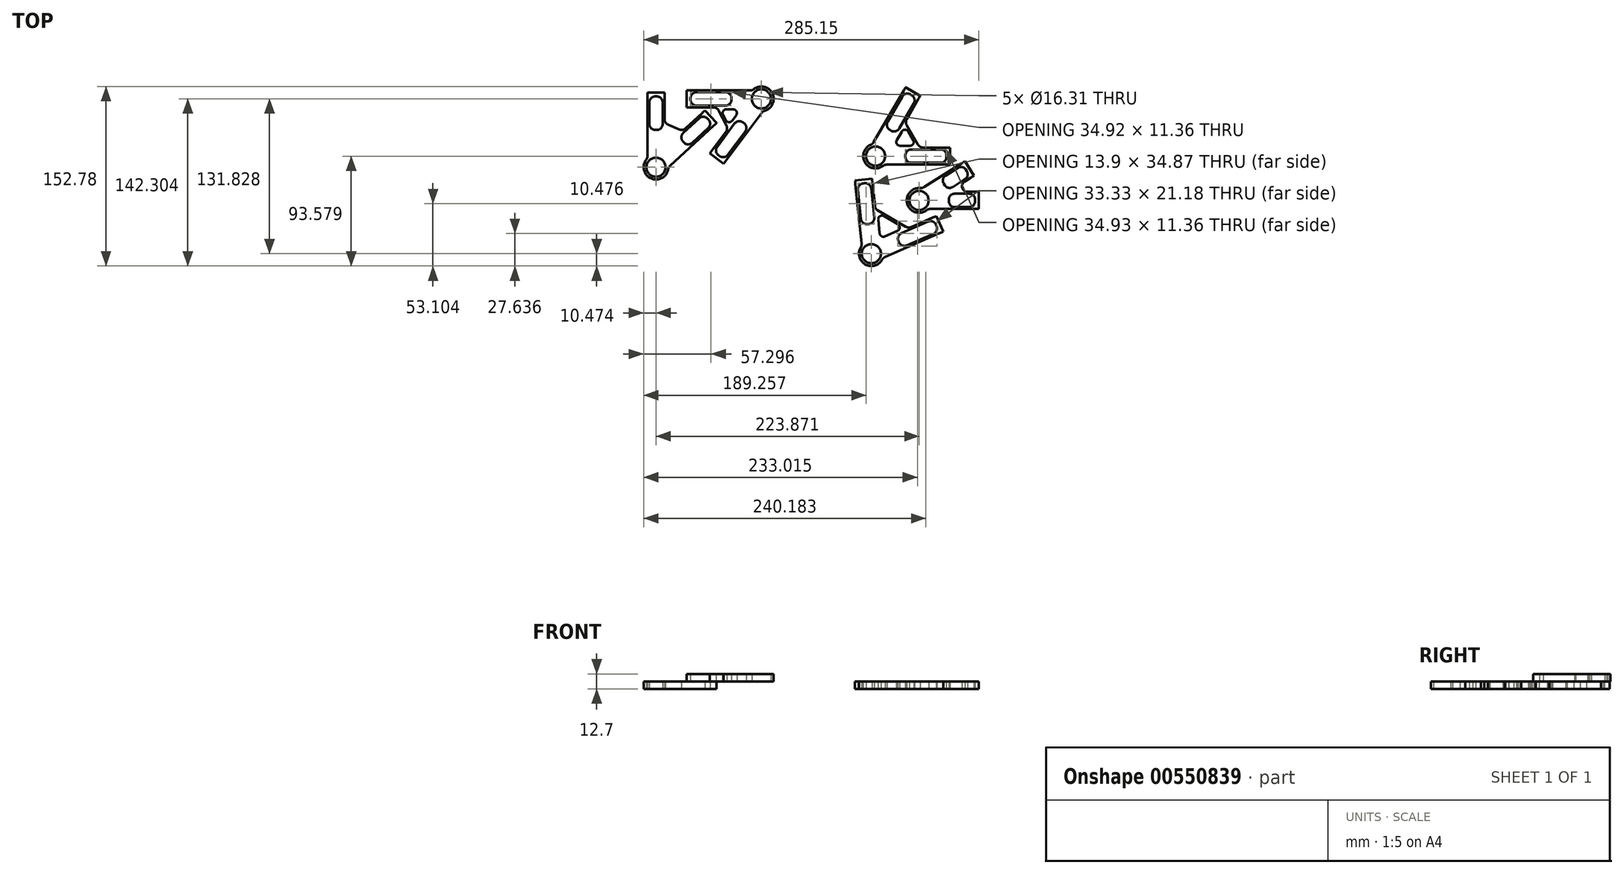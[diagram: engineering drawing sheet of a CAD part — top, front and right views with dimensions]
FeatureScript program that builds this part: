
annotation { "Feature Type Name" : "Feature", "Feature Type Description" : "" }
export const myFeature = defineFeature(function(context is Context, id is Id, definition is map)
    precondition{}
    {
        {
            var Q0;
            Q0=qCreatedBy(makeId("Top.planeOp"),FACE);
            var sketch = newSketch(context, id + "F0", { "sketchPlane" : qUnion([Q0])});
            skLineSegment(sketch, "E0", {"start": v(266.5, 117.67) * mm, "end": v(266.5, 132.21) * mm});
            skLineSegment(sketch, "E1", {"start": v(262.48, 146.06) * mm, "end": v(254.68, 158.33) * mm});
            skLineSegment(sketch, "E2", {"start": v(236.2, 98.34) * mm, "end": v(230.38, 111.66) * mm});
            skLineSegment(sketch, "E3", {"start": v(175.69, 143.49) * mm, "end": v(161.23, 141.97) * mm});
            skLineSegment(sketch, "E4", {"start": v(242.18, 155.4) * mm, "end": v(242.18, 169.95) * mm});
            skLineSegment(sketch, "E5", {"start": v(216.73, 214.04) * mm, "end": v(204.14, 221.3) * mm});
            skLineSegment(sketch, "E6", {"start": v(-0.9, 216.73) * mm, "end": v(-15.44, 216.73) * mm});
            skLineSegment(sketch, "E7", {"start": v(43.43, 190.95) * mm, "end": v(33.57, 201.64) * mm});
            skLineSegment(sketch, "E8", {"start": v(185.25, 66.4) * mm, "end": v(185.8, 67.33) * mm});
            skLineSegment(sketch, "E9", {"start": v(185.8, 67.33) * mm, "end": v(186.27, 68.16) * mm});
            skLineSegment(sketch, "E10", {"start": v(186.27, 68.16) * mm, "end": v(186.62, 68.77) * mm});
            skLineSegment(sketch, "E11", {"start": v(186.62, 68.77) * mm, "end": v(186.81, 69.1) * mm});
            skLineSegment(sketch, "E12", {"start": v(186.81, 69.1) * mm, "end": v(186.84, 69.14) * mm});
            skLineSegment(sketch, "E13", {"start": v(254.51, 141) * mm, "end": v(259.8, 144.36) * mm});
            skLineSegment(sketch, "E14", {"start": v(263.33, 132.21) * mm, "end": v(257.07, 132.21) * mm});
            skLineSegment(sketch, "E15", {"start": v(245.87, 130.63) * mm, "end": v(258.57, 130.63) * mm});
            skLineSegment(sketch, "E16", {"start": v(241.1, 124.02) * mm, "end": v(241.1, 125.86) * mm});
            skLineSegment(sketch, "E17", {"start": v(258.57, 119.26) * mm, "end": v(245.87, 119.26) * mm});
            skLineSegment(sketch, "E18", {"start": v(225.59, 117.67) * mm, "end": v(263.33, 117.67) * mm});
            skLineSegment(sketch, "E19", {"start": v(252, 156.63) * mm, "end": v(220.15, 136.38) * mm});
            skLineSegment(sketch, "E20", {"start": v(238.11, 145.92) * mm, "end": v(248.83, 152.73) * mm});
            skLineSegment(sketch, "E21", {"start": v(237.63, 137.8) * mm, "end": v(236.65, 139.34) * mm});
            skLineSegment(sketch, "E22", {"start": v(254.93, 143.14) * mm, "end": v(244.2, 136.33) * mm});
            skLineSegment(sketch, "E23", {"start": v(263.33, 124.02) * mm, "end": v(263.33, 125.86) * mm});
            skLineSegment(sketch, "E24", {"start": v(266.5, 132.21) * mm, "end": v(263.33, 132.21) * mm});
            skLineSegment(sketch, "E25", {"start": v(266.5, 117.67) * mm, "end": v(263.33, 117.67) * mm});
            skLineSegment(sketch, "E26", {"start": v(256.4, 149.71) * mm, "end": v(255.4, 151.27) * mm});
            skLineSegment(sketch, "E27", {"start": v(262.48, 146.06) * mm, "end": v(262.44, 146.03) * mm});
            skLineSegment(sketch, "E28", {"start": v(262.44, 146.03) * mm, "end": v(262.12, 145.83) * mm});
            skLineSegment(sketch, "E29", {"start": v(262.12, 145.83) * mm, "end": v(261.52, 145.45) * mm});
            skLineSegment(sketch, "E30", {"start": v(261.52, 145.45) * mm, "end": v(260.71, 144.94) * mm});
            skLineSegment(sketch, "E31", {"start": v(260.71, 144.94) * mm, "end": v(259.8, 144.36) * mm});
            skLineSegment(sketch, "E32", {"start": v(252, 156.63) * mm, "end": v(252.92, 157.2) * mm});
            skLineSegment(sketch, "E33", {"start": v(252.92, 157.2) * mm, "end": v(253.72, 157.72) * mm});
            skLineSegment(sketch, "E34", {"start": v(253.72, 157.72) * mm, "end": v(254.32, 158.1) * mm});
            skLineSegment(sketch, "E35", {"start": v(254.32, 158.1) * mm, "end": v(254.64, 158.3) * mm});
            skLineSegment(sketch, "E36", {"start": v(254.64, 158.3) * mm, "end": v(254.68, 158.33) * mm});
            skLineSegment(sketch, "E37", {"start": v(236.2, 98.34) * mm, "end": v(236.15, 98.32) * mm});
            skLineSegment(sketch, "E38", {"start": v(236.15, 98.32) * mm, "end": v(235.8, 98.17) * mm});
            skLineSegment(sketch, "E39", {"start": v(235.8, 98.17) * mm, "end": v(235.16, 97.88) * mm});
            skLineSegment(sketch, "E40", {"start": v(235.16, 97.88) * mm, "end": v(234.28, 97.5) * mm});
            skLineSegment(sketch, "E41", {"start": v(234.28, 97.5) * mm, "end": v(233.29, 97.07) * mm});
            skLineSegment(sketch, "E42", {"start": v(230.62, 103.18) * mm, "end": v(230.14, 104.28) * mm});
            skLineSegment(sketch, "E43", {"start": v(227.47, 110.39) * mm, "end": v(228.46, 110.82) * mm});
            skLineSegment(sketch, "E44", {"start": v(228.46, 110.82) * mm, "end": v(229.34, 111.2) * mm});
            skLineSegment(sketch, "E45", {"start": v(229.34, 111.2) * mm, "end": v(229.99, 111.49) * mm});
            skLineSegment(sketch, "E46", {"start": v(229.99, 111.49) * mm, "end": v(230.33, 111.64) * mm});
            skLineSegment(sketch, "E47", {"start": v(230.33, 111.64) * mm, "end": v(230.38, 111.66) * mm});
            skLineSegment(sketch, "E48", {"start": v(161.56, 138.81) * mm, "end": v(166.88, 88.23) * mm});
            skLineSegment(sketch, "E49", {"start": v(166.26, 109.3) * mm, "end": v(163.67, 133.92) * mm});
            skLineSegment(sketch, "E50", {"start": v(171.84, 104.77) * mm, "end": v(173.04, 104.9) * mm});
            skLineSegment(sketch, "E51", {"start": v(174.97, 135.11) * mm, "end": v(177.56, 110.48) * mm});
            skLineSegment(sketch, "E52", {"start": v(178.13, 120.24) * mm, "end": v(176.02, 140.33) * mm});
            skLineSegment(sketch, "E53", {"start": v(204.37, 102.57) * mm, "end": v(180.63, 116.38) * mm});
            skLineSegment(sketch, "E54", {"start": v(200.75, 96.99) * mm, "end": v(223.45, 106.9) * mm});
            skLineSegment(sketch, "E55", {"start": v(198.13, 90.3) * mm, "end": v(198.61, 89.2) * mm});
            skLineSegment(sketch, "E56", {"start": v(228, 96.49) * mm, "end": v(205.3, 86.57) * mm});
            skLineSegment(sketch, "E57", {"start": v(185.72, 111.58) * mm, "end": v(197.68, 104.62) * mm});
            skLineSegment(sketch, "E58", {"start": v(182.19, 96.85) * mm, "end": v(180.96, 108.5) * mm});
            skLineSegment(sketch, "E59", {"start": v(197.35, 98.97) * mm, "end": v(186.62, 94.28) * mm});
            skLineSegment(sketch, "E60", {"start": v(227.47, 110.39) * mm, "end": v(208.95, 102.3) * mm});
            skLineSegment(sketch, "E61", {"start": v(186.68, 76.7) * mm, "end": v(233.29, 97.07) * mm});
            skLineSegment(sketch, "E62", {"start": v(175.69, 143.49) * mm, "end": v(175.7, 143.44) * mm});
            skLineSegment(sketch, "E63", {"start": v(175.7, 143.44) * mm, "end": v(175.73, 143.07) * mm});
            skLineSegment(sketch, "E64", {"start": v(175.73, 143.07) * mm, "end": v(175.8, 142.36) * mm});
            skLineSegment(sketch, "E65", {"start": v(175.8, 142.36) * mm, "end": v(175.9, 141.41) * mm});
            skLineSegment(sketch, "E66", {"start": v(175.9, 141.41) * mm, "end": v(176.02, 140.33) * mm});
            skLineSegment(sketch, "E67", {"start": v(169.4, 139.63) * mm, "end": v(168.2, 139.5) * mm});
            skLineSegment(sketch, "E68", {"start": v(161.56, 138.81) * mm, "end": v(161.45, 139.9) * mm});
            skLineSegment(sketch, "E69", {"start": v(161.45, 139.9) * mm, "end": v(161.35, 140.84) * mm});
            skLineSegment(sketch, "E70", {"start": v(161.35, 140.84) * mm, "end": v(161.28, 141.55) * mm});
            skLineSegment(sketch, "E71", {"start": v(161.28, 141.55) * mm, "end": v(161.24, 141.92) * mm});
            skLineSegment(sketch, "E72", {"start": v(161.24, 141.92) * mm, "end": v(161.23, 141.97) * mm});
            skLineSegment(sketch, "E73", {"start": v(242.18, 155.4) * mm, "end": v(239, 155.4) * mm});
            skLineSegment(sketch, "E74", {"start": v(239, 162.08) * mm, "end": v(239, 163.28) * mm});
            skLineSegment(sketch, "E75", {"start": v(239, 169.95) * mm, "end": v(242.18, 169.95) * mm});
            skLineSegment(sketch, "E76", {"start": v(202.55, 218.56) * mm, "end": v(177.12, 174.5) * mm});
            skLineSegment(sketch, "E77", {"start": v(189, 191.92) * mm, "end": v(201.38, 213.36) * mm});
            skLineSegment(sketch, "E78", {"start": v(190.86, 184.98) * mm, "end": v(191.9, 184.38) * mm});
            skLineSegment(sketch, "E79", {"start": v(211.22, 207.68) * mm, "end": v(198.84, 186.23) * mm});
            skLineSegment(sketch, "E80", {"start": v(205.22, 194.1) * mm, "end": v(215.14, 211.29) * mm});
            skLineSegment(sketch, "E81", {"start": v(214.76, 172.49) * mm, "end": v(205.22, 189.02) * mm});
            skLineSegment(sketch, "E82", {"start": v(209.16, 168.36) * mm, "end": v(233.93, 168.36) * mm});
            skLineSegment(sketch, "E83", {"start": v(204.08, 163.28) * mm, "end": v(204.08, 162.08) * mm});
            skLineSegment(sketch, "E84", {"start": v(233.93, 157) * mm, "end": v(209.16, 157) * mm});
            skLineSegment(sketch, "E85", {"start": v(206.5, 183.62) * mm, "end": v(210.73, 176.3) * mm});
            skLineSegment(sketch, "E86", {"start": v(196.77, 176.3) * mm, "end": v(201, 183.62) * mm});
            skLineSegment(sketch, "E87", {"start": v(207.98, 171.54) * mm, "end": v(199.52, 171.54) * mm});
            skLineSegment(sketch, "E88", {"start": v(239, 169.95) * mm, "end": v(219.16, 169.95) * mm});
            skLineSegment(sketch, "E89", {"start": v(188.14, 155.4) * mm, "end": v(239, 155.4) * mm});
            skLineSegment(sketch, "E90", {"start": v(216.73, 214.04) * mm, "end": v(216.7, 214) * mm});
            skLineSegment(sketch, "E91", {"start": v(216.7, 214) * mm, "end": v(216.51, 213.67) * mm});
            skLineSegment(sketch, "E92", {"start": v(216.51, 213.67) * mm, "end": v(216.16, 213.05) * mm});
            skLineSegment(sketch, "E93", {"start": v(216.16, 213.05) * mm, "end": v(215.68, 212.23) * mm});
            skLineSegment(sketch, "E94", {"start": v(215.68, 212.23) * mm, "end": v(215.14, 211.29) * mm});
            skLineSegment(sketch, "E95", {"start": v(209.36, 214.62) * mm, "end": v(208.32, 215.22) * mm});
            skLineSegment(sketch, "E96", {"start": v(202.55, 218.56) * mm, "end": v(203.1, 219.5) * mm});
            skLineSegment(sketch, "E97", {"start": v(203.1, 219.5) * mm, "end": v(203.57, 220.32) * mm});
            skLineSegment(sketch, "E98", {"start": v(203.57, 220.32) * mm, "end": v(203.92, 220.94) * mm});
            skLineSegment(sketch, "E99", {"start": v(203.92, 220.94) * mm, "end": v(204.11, 221.26) * mm});
            skLineSegment(sketch, "E100", {"start": v(204.11, 221.26) * mm, "end": v(204.14, 221.3) * mm});
            skLineSegment(sketch, "E101", {"start": v(-15.44, 213.56) * mm, "end": v(-15.44, 162.7) * mm});
            skLineSegment(sketch, "E102", {"start": v(-13.85, 190.06) * mm, "end": v(-13.85, 208.48) * mm});
            skLineSegment(sketch, "E103", {"start": v(-8.77, 184.98) * mm, "end": v(-7.56, 184.98) * mm});
            skLineSegment(sketch, "E104", {"start": v(-2.48, 208.48) * mm, "end": v(-2.48, 190.06) * mm});
            skLineSegment(sketch, "E105", {"start": v(-0.9, 194.1) * mm, "end": v(-0.9, 213.56) * mm});
            skLineSegment(sketch, "E106", {"start": v(11.45, 185.37) * mm, "end": v(2.15, 189.44) * mm});
            skLineSegment(sketch, "E107", {"start": v(31.24, 199.48) * mm, "end": v(16.94, 186.29) * mm});
            skLineSegment(sketch, "E108", {"start": v(15.05, 182.38) * mm, "end": v(28.58, 194.87) * mm});
            skLineSegment(sketch, "E109", {"start": v(14.76, 175.2) * mm, "end": v(15.58, 174.32) * mm});
            skLineSegment(sketch, "E110", {"start": v(36.29, 186.52) * mm, "end": v(22.75, 174.03) * mm});
            skLineSegment(sketch, "E111", {"start": v(3.72, 154.3) * mm, "end": v(41.1, 188.8) * mm});
            skLineSegment(sketch, "E112", {"start": v(-15.44, 213.56) * mm, "end": v(-15.44, 216.73) * mm});
            skLineSegment(sketch, "E113", {"start": v(-0.9, 216.73) * mm, "end": v(-0.9, 213.56) * mm});
            skLineSegment(sketch, "E114", {"start": v(-7.56, 213.56) * mm, "end": v(-8.77, 213.56) * mm});
            skLineSegment(sketch, "E115", {"start": v(36.58, 193.7) * mm, "end": v(35.76, 194.58) * mm});
            skLineSegment(sketch, "E116", {"start": v(31.24, 199.48) * mm, "end": v(32.04, 200.22) * mm});
            skLineSegment(sketch, "E117", {"start": v(32.04, 200.22) * mm, "end": v(32.74, 200.87) * mm});
            skLineSegment(sketch, "E118", {"start": v(32.74, 200.87) * mm, "end": v(33.26, 201.35) * mm});
            skLineSegment(sketch, "E119", {"start": v(33.26, 201.35) * mm, "end": v(33.54, 201.6) * mm});
            skLineSegment(sketch, "E120", {"start": v(33.54, 201.6) * mm, "end": v(33.57, 201.64) * mm});
            skLineSegment(sketch, "E121", {"start": v(43.43, 190.95) * mm, "end": v(43.4, 190.92) * mm});
            skLineSegment(sketch, "E122", {"start": v(43.4, 190.92) * mm, "end": v(43.12, 190.66) * mm});
            skLineSegment(sketch, "E123", {"start": v(43.12, 190.66) * mm, "end": v(42.6, 190.18) * mm});
            skLineSegment(sketch, "E124", {"start": v(42.6, 190.18) * mm, "end": v(41.9, 189.53) * mm});
            skLineSegment(sketch, "E125", {"start": v(41.9, 189.53) * mm, "end": v(41.1, 188.8) * mm});
            skCircle(sketch, "E126", {"center": v(-8.17, 153.23) * mm, "radius": 8.16 * mm});
            skArc(sketch, "E127", {"start": v(254.93, 143.14) * mm, "mid": v(257.02, 146.12) * mm, "end": v(256.4, 149.71) * mm});
            skArc(sketch, "E128", {"start": v(254.51, 141) * mm, "mid": v(252.5, 135.65) * mm, "end": v(257.07, 132.21) * mm});
            skArc(sketch, "E129", {"start": v(263.33, 125.86) * mm, "mid": v(261.94, 129.23) * mm, "end": v(258.57, 130.63) * mm});
            skArc(sketch, "E130", {"start": v(245.87, 130.63) * mm, "mid": v(242.5, 129.23) * mm, "end": v(241.1, 125.86) * mm});
            skArc(sketch, "E131", {"start": v(241.1, 124.02) * mm, "mid": v(242.5, 120.66) * mm, "end": v(245.87, 119.26) * mm});
            skArc(sketch, "E132", {"start": v(258.57, 119.26) * mm, "mid": v(261.94, 120.66) * mm, "end": v(263.33, 124.02) * mm});
            skArc(sketch, "E133", {"start": v(225.59, 117.67) * mm, "mid": v(223.63, 117.36) * mm, "end": v(221.86, 116.46) * mm});
            skArc(sketch, "E134", {"start": v(216.35, 135.4) * mm, "mid": v(205.64, 122.02) * mm, "end": v(221.86, 116.46) * mm});
            skArc(sketch, "E135", {"start": v(216.35, 135.4) * mm, "mid": v(218.33, 135.6) * mm, "end": v(220.15, 136.38) * mm});
            skArc(sketch, "E136", {"start": v(255.4, 151.27) * mm, "mid": v(252.42, 153.36) * mm, "end": v(248.83, 152.73) * mm});
            skArc(sketch, "E137", {"start": v(238.11, 145.92) * mm, "mid": v(236.02, 142.94) * mm, "end": v(236.65, 139.34) * mm});
            skArc(sketch, "E138", {"start": v(237.63, 137.8) * mm, "mid": v(240.62, 135.7) * mm, "end": v(244.2, 136.33) * mm});
            skArc(sketch, "E139", {"start": v(166.16, 85.04) * mm, "mid": v(166.78, 86.58) * mm, "end": v(166.88, 88.23) * mm});
            skArc(sketch, "E140", {"start": v(168.2, 139.5) * mm, "mid": v(164.78, 137.65) * mm, "end": v(163.67, 133.92) * mm});
            skArc(sketch, "E141", {"start": v(166.26, 109.3) * mm, "mid": v(168.12, 105.88) * mm, "end": v(171.84, 104.77) * mm});
            skArc(sketch, "E142", {"start": v(173.04, 104.9) * mm, "mid": v(176.46, 106.76) * mm, "end": v(177.56, 110.48) * mm});
            skArc(sketch, "E143", {"start": v(174.97, 135.11) * mm, "mid": v(173.12, 138.53) * mm, "end": v(169.4, 139.63) * mm});
            skArc(sketch, "E144", {"start": v(178.13, 120.24) * mm, "mid": v(178.92, 118.01) * mm, "end": v(180.63, 116.38) * mm});
            skArc(sketch, "E145", {"start": v(204.37, 102.57) * mm, "mid": v(206.63, 101.88) * mm, "end": v(208.95, 102.3) * mm});
            skArc(sketch, "E146", {"start": v(200.75, 96.99) * mm, "mid": v(198.06, 94.18) * mm, "end": v(198.13, 90.3) * mm});
            skArc(sketch, "E147", {"start": v(198.61, 89.2) * mm, "mid": v(201.42, 86.5) * mm, "end": v(205.3, 86.57) * mm});
            skArc(sketch, "E148", {"start": v(228, 96.49) * mm, "mid": v(230.7, 99.29) * mm, "end": v(230.62, 103.18) * mm});
            skArc(sketch, "E149", {"start": v(186.68, 76.7) * mm, "mid": v(185.3, 75.8) * mm, "end": v(184.27, 74.5) * mm});
            skArc(sketch, "E150", {"start": v(166.16, 85.04) * mm, "mid": v(169.83, 70.52) * mm, "end": v(184.27, 74.5) * mm});
            skArc(sketch, "E151", {"start": v(197.35, 98.97) * mm, "mid": v(199.25, 101.7) * mm, "end": v(197.68, 104.62) * mm});
            skArc(sketch, "E152", {"start": v(185.72, 111.58) * mm, "mid": v(182.4, 111.5) * mm, "end": v(180.96, 108.5) * mm});
            skArc(sketch, "E153", {"start": v(182.19, 96.85) * mm, "mid": v(183.75, 94.44) * mm, "end": v(186.62, 94.28) * mm});
            skArc(sketch, "E154", {"start": v(230.14, 104.28) * mm, "mid": v(227.33, 106.97) * mm, "end": v(223.45, 106.9) * mm});
            skCircle(sketch, "E155", {"center": v(178.68, 162.68) * mm, "radius": 8.16 * mm});
            skCircle(sketch, "E156", {"center": v(215.7, 124.94) * mm, "radius": 8.16 * mm});
            skArc(sketch, "E157", {"start": v(174.66, 172.36) * mm, "mid": v(176.07, 173.23) * mm, "end": v(177.12, 174.5) * mm});
            skArc(sketch, "E158", {"start": v(208.32, 215.22) * mm, "mid": v(204.47, 215.73) * mm, "end": v(201.38, 213.36) * mm});
            skArc(sketch, "E159", {"start": v(189, 191.92) * mm, "mid": v(188.5, 188.06) * mm, "end": v(190.86, 184.98) * mm});
            skArc(sketch, "E160", {"start": v(191.9, 184.38) * mm, "mid": v(195.76, 183.87) * mm, "end": v(198.84, 186.23) * mm});
            skArc(sketch, "E161", {"start": v(211.22, 207.68) * mm, "mid": v(211.73, 211.54) * mm, "end": v(209.36, 214.62) * mm});
            skArc(sketch, "E162", {"start": v(205.22, 194.1) * mm, "mid": v(204.54, 191.56) * mm, "end": v(205.22, 189.02) * mm});
            skArc(sketch, "E163", {"start": v(214.76, 172.49) * mm, "mid": v(216.62, 170.63) * mm, "end": v(219.16, 169.95) * mm});
            skArc(sketch, "E164", {"start": v(239, 163.28) * mm, "mid": v(237.52, 166.87) * mm, "end": v(233.93, 168.36) * mm});
            skArc(sketch, "E165", {"start": v(209.16, 168.36) * mm, "mid": v(205.57, 166.87) * mm, "end": v(204.08, 163.28) * mm});
            skArc(sketch, "E166", {"start": v(204.08, 162.08) * mm, "mid": v(205.57, 158.49) * mm, "end": v(209.16, 157) * mm});
            skArc(sketch, "E167", {"start": v(233.93, 157) * mm, "mid": v(237.52, 158.49) * mm, "end": v(239, 162.08) * mm});
            skArc(sketch, "E168", {"start": v(188.14, 155.4) * mm, "mid": v(186.51, 155.14) * mm, "end": v(185.05, 154.36) * mm});
            skArc(sketch, "E169", {"start": v(174.66, 172.36) * mm, "mid": v(169.6, 157.44) * mm, "end": v(185.05, 154.36) * mm});
            skArc(sketch, "E170", {"start": v(207.98, 171.54) * mm, "mid": v(210.73, 173.12) * mm, "end": v(210.73, 176.3) * mm});
            skArc(sketch, "E171", {"start": v(206.5, 183.62) * mm, "mid": v(203.75, 185.2) * mm, "end": v(201, 183.62) * mm});
            skArc(sketch, "E172", {"start": v(196.77, 176.3) * mm, "mid": v(196.77, 173.12) * mm, "end": v(199.52, 171.54) * mm});
            skCircle(sketch, "E173", {"center": v(175.1, 79.58) * mm, "radius": 8.16 * mm});
            skArc(sketch, "E174", {"start": v(-16.48, 159.6) * mm, "mid": v(-15.7, 161.06) * mm, "end": v(-15.44, 162.7) * mm});
            skArc(sketch, "E175", {"start": v(-8.77, 213.56) * mm, "mid": v(-12.36, 212.07) * mm, "end": v(-13.85, 208.48) * mm});
            skArc(sketch, "E176", {"start": v(-13.85, 190.06) * mm, "mid": v(-12.36, 186.47) * mm, "end": v(-8.77, 184.98) * mm});
            skArc(sketch, "E177", {"start": v(-7.56, 184.98) * mm, "mid": v(-3.97, 186.47) * mm, "end": v(-2.48, 190.06) * mm});
            skArc(sketch, "E178", {"start": v(-2.48, 208.48) * mm, "mid": v(-3.97, 212.07) * mm, "end": v(-7.56, 213.56) * mm});
            skArc(sketch, "E179", {"start": v(-0.9, 194.1) * mm, "mid": v(-0.07, 191.32) * mm, "end": v(2.15, 189.44) * mm});
            skArc(sketch, "E180", {"start": v(11.45, 185.37) * mm, "mid": v(14.33, 185.01) * mm, "end": v(16.94, 186.29) * mm});
            skArc(sketch, "E181", {"start": v(35.76, 194.58) * mm, "mid": v(32.23, 196.21) * mm, "end": v(28.58, 194.87) * mm});
            skArc(sketch, "E182", {"start": v(15.05, 182.38) * mm, "mid": v(13.42, 178.85) * mm, "end": v(14.76, 175.2) * mm});
            skArc(sketch, "E183", {"start": v(15.58, 174.32) * mm, "mid": v(19.1, 172.69) * mm, "end": v(22.75, 174.03) * mm});
            skArc(sketch, "E184", {"start": v(36.29, 186.52) * mm, "mid": v(37.92, 190.05) * mm, "end": v(36.58, 193.7) * mm});
            skArc(sketch, "E185", {"start": v(3.72, 154.3) * mm, "mid": v(2.7, 153) * mm, "end": v(2.16, 151.44) * mm});
            skArc(sketch, "E186", {"start": v(-16.48, 159.6) * mm, "mid": v(-12.37, 143.63) * mm, "end": v(2.16, 151.44) * mm});
            skSolve(sketch);
        }
        {
            var Q0;
            Q0=makeQuery(id+"F0.imprint","IMPRINT",FACE,{"disambiguationData":[TD([[makeQuery(id+"F0.imprint","IMPRINT",EDGE,{"derivedFrom":sQuery(id+"F0.wireOp",EDGE,"E6")}),1.0]])]});
            var Q1;
            Q1=makeQuery(id+"F0.imprint","IMPRINT",FACE,{"disambiguationData":[TD([[makeQuery(id+"F0.imprint","IMPRINT",EDGE,{"derivedFrom":sQuery(id+"F0.wireOp",EDGE,"E4")}),1.0]])]});
            var Q2;
            Q2=makeQuery(id+"F0.imprint","IMPRINT",FACE,{"disambiguationData":[TD([[makeQuery(id+"F0.imprint","IMPRINT",EDGE,{"derivedFrom":sQuery(id+"F0.wireOp",EDGE,"E0")}),1.0]])]});
            var Q3;
            Q3=makeQuery(id+"F0.imprint","IMPRINT",FACE,{"disambiguationData":[TD([[makeQuery(id+"F0.imprint","IMPRINT",EDGE,{"derivedFrom":sQuery(id+"F0.wireOp",EDGE,"E2")}),1.0]])]});
            extrude(context, id + "F1", {"entities" : qUnion([Q0, Q1, Q2, Q3]), "depth" : 6.35 * mm, "offsetDistance" : 25.4 * mm});
        }
        {
            var Q0;
            Q0=makeQuery(id+"F1.opExtrude","CAP_FACE",FACE,{"disambiguationData":[OSD([sQuery(id+"F0.wireOp",EDGE,"E6"),sQuery(id+"F0.wireOp",EDGE,"E7"),sQuery(id+"F0.wireOp",EDGE,"E101"),sQuery(id+"F0.wireOp",EDGE,"E102"),sQuery(id+"F0.wireOp",EDGE,"E103"),sQuery(id+"F0.wireOp",EDGE,"E104"),sQuery(id+"F0.wireOp",EDGE,"E105"),sQuery(id+"F0.wireOp",EDGE,"E106"),sQuery(id+"F0.wireOp",EDGE,"E107"),sQuery(id+"F0.wireOp",EDGE,"E108"),sQuery(id+"F0.wireOp",EDGE,"E109"),sQuery(id+"F0.wireOp",EDGE,"E110"),sQuery(id+"F0.wireOp",EDGE,"E111"),sQuery(id+"F0.wireOp",EDGE,"E112"),sQuery(id+"F0.wireOp",EDGE,"E113"),sQuery(id+"F0.wireOp",EDGE,"E114"),sQuery(id+"F0.wireOp",EDGE,"E115"),sQuery(id+"F0.wireOp",EDGE,"E116"),sQuery(id+"F0.wireOp",EDGE,"E117"),sQuery(id+"F0.wireOp",EDGE,"E118"),sQuery(id+"F0.wireOp",EDGE,"E119"),sQuery(id+"F0.wireOp",EDGE,"E120"),sQuery(id+"F0.wireOp",EDGE,"E121"),sQuery(id+"F0.wireOp",EDGE,"E122"),sQuery(id+"F0.wireOp",EDGE,"E123"),sQuery(id+"F0.wireOp",EDGE,"E124"),sQuery(id+"F0.wireOp",EDGE,"E125"),sQuery(id+"F0.wireOp",EDGE,"E126"),sQuery(id+"F0.wireOp",EDGE,"E174"),sQuery(id+"F0.wireOp",EDGE,"E175"),sQuery(id+"F0.wireOp",EDGE,"E176"),sQuery(id+"F0.wireOp",EDGE,"E177"),sQuery(id+"F0.wireOp",EDGE,"E178"),sQuery(id+"F0.wireOp",EDGE,"E179"),sQuery(id+"F0.wireOp",EDGE,"E180"),sQuery(id+"F0.wireOp",EDGE,"E181"),sQuery(id+"F0.wireOp",EDGE,"E182"),sQuery(id+"F0.wireOp",EDGE,"E183"),sQuery(id+"F0.wireOp",EDGE,"E184"),sQuery(id+"F0.wireOp",EDGE,"E185"),sQuery(id+"F0.wireOp",EDGE,"E186")])],"isStart":false});
            var sketch = newSketch(context, id + "F2", { "sketchPlane" : qUnion([Q0])});
            skLineSegment(sketch, "E187", {"start": v(159.92, 33.8) * mm, "end": v(159.92, 48.35) * mm});
            skLineSegment(sketch, "E188", {"start": v(155.9, 62.2) * mm, "end": v(148.1, 74.46) * mm});
            skLineSegment(sketch, "E189", {"start": v(261.52, 33.8) * mm, "end": v(261.52, 48.35) * mm});
            skLineSegment(sketch, "E190", {"start": v(257.5, 62.2) * mm, "end": v(249.7, 74.46) * mm});
            skLineSegment(sketch, "E191", {"start": v(251.83, -49.98) * mm, "end": v(246, -36.66) * mm});
            skLineSegment(sketch, "E192", {"start": v(191.32, -4.83) * mm, "end": v(176.86, -6.35) * mm});
            skLineSegment(sketch, "E193", {"start": v(172.7, -48.13) * mm, "end": v(166.87, -34.8) * mm});
            skLineSegment(sketch, "E194", {"start": v(112.18, -2.97) * mm, "end": v(97.72, -4.5) * mm});
            skLineSegment(sketch, "E195", {"start": v(123.28, 3.25) * mm, "end": v(123.28, 17.78) * mm});
            skLineSegment(sketch, "E196", {"start": v(97.83, 61.87) * mm, "end": v(85.24, 69.14) * mm});
            skLineSegment(sketch, "E197", {"start": v(224.88, 3.25) * mm, "end": v(224.88, 17.78) * mm});
            skLineSegment(sketch, "E198", {"start": v(199.43, 61.87) * mm, "end": v(186.84, 69.14) * mm});
            skLineSegment(sketch, "E199", {"start": v(37.76, -59) * mm, "end": v(49.4, -67.72) * mm});
            skLineSegment(sketch, "E200", {"start": v(18.15, -5.27) * mm, "end": v(18.15, -19.8) * mm});
            skLineSegment(sketch, "E201", {"start": v(20.34, 12.77) * mm, "end": v(31.97, 4.06) * mm});
            skLineSegment(sketch, "E202", {"start": v(0.72, 66.5) * mm, "end": v(0.72, 51.97) * mm});
            skLineSegment(sketch, "E203", {"start": v(-18.2, 64.57) * mm, "end": v(-32.73, 64.57) * mm});
            skLineSegment(sketch, "E204", {"start": v(26.13, 38.79) * mm, "end": v(16.27, 49.47) * mm});
            skLineSegment(sketch, "E205", {"start": v(-0.77, -7.21) * mm, "end": v(-15.3, -7.21) * mm});
            skLineSegment(sketch, "E206", {"start": v(43.56, -33) * mm, "end": v(33.7, -22.3) * mm});
            skLineSegment(sketch, "E207", {"start": v(177.22, 185.97) * mm, "end": v(177.22, 200.51) * mm});
            skLineSegment(sketch, "E208", {"start": v(173.2, 214.36) * mm, "end": v(165.4, 226.63) * mm});
            skLineSegment(sketch, "E209", {"start": v(266.5, 117.67) * mm, "end": v(266.5, 132.21) * mm});
            skLineSegment(sketch, "E210", {"start": v(262.48, 146.06) * mm, "end": v(254.68, 158.33) * mm});
            skLineSegment(sketch, "E211", {"start": v(236.2, 98.34) * mm, "end": v(230.38, 111.66) * mm});
            skLineSegment(sketch, "E212", {"start": v(175.69, 143.49) * mm, "end": v(161.23, 141.97) * mm});
            skLineSegment(sketch, "E213", {"start": v(157.06, 100.2) * mm, "end": v(151.24, 113.51) * mm});
            skLineSegment(sketch, "E214", {"start": v(96.55, 145.34) * mm, "end": v(82.1, 143.82) * mm});
            skLineSegment(sketch, "E215", {"start": v(140.58, 155.4) * mm, "end": v(140.58, 169.95) * mm});
            skLineSegment(sketch, "E216", {"start": v(115.13, 214.04) * mm, "end": v(102.54, 221.3) * mm});
            skLineSegment(sketch, "E217", {"start": v(242.18, 155.4) * mm, "end": v(242.18, 169.95) * mm});
            skLineSegment(sketch, "E218", {"start": v(216.73, 214.04) * mm, "end": v(204.14, 221.3) * mm});
            skLineSegment(sketch, "E219", {"start": v(22.13, 89.31) * mm, "end": v(33.77, 80.6) * mm});
            skLineSegment(sketch, "E220", {"start": v(2.51, 143.05) * mm, "end": v(2.51, 128.5) * mm});
            skLineSegment(sketch, "E221", {"start": v(37.63, 164.94) * mm, "end": v(49.27, 156.22) * mm});
            skLineSegment(sketch, "E222", {"start": v(18.02, 218.67) * mm, "end": v(18.02, 204.13) * mm});
            skLineSegment(sketch, "E223", {"start": v(-0.9, 216.73) * mm, "end": v(-15.44, 216.73) * mm});
            skLineSegment(sketch, "E224", {"start": v(147.93, 57.13) * mm, "end": v(153.21, 60.49) * mm});
            skLineSegment(sketch, "E225", {"start": v(156.74, 48.35) * mm, "end": v(150.48, 48.35) * mm});
            skLineSegment(sketch, "E226", {"start": v(43.43, 190.95) * mm, "end": v(33.57, 201.64) * mm});
            skLineSegment(sketch, "E227", {"start": v(139.28, 46.76) * mm, "end": v(151.98, 46.76) * mm});
            skLineSegment(sketch, "E228", {"start": v(134.52, 40.16) * mm, "end": v(134.52, 42) * mm});
            skLineSegment(sketch, "E229", {"start": v(151.98, 35.4) * mm, "end": v(139.28, 35.4) * mm});
            skLineSegment(sketch, "E230", {"start": v(-16.4, 141.1) * mm, "end": v(-30.94, 141.1) * mm});
            skLineSegment(sketch, "E231", {"start": v(119, 33.8) * mm, "end": v(156.74, 33.8) * mm});
            skLineSegment(sketch, "E232", {"start": v(145.41, 72.76) * mm, "end": v(113.56, 52.51) * mm});
            skLineSegment(sketch, "E233", {"start": v(27.93, 115.33) * mm, "end": v(18.07, 126.01) * mm});
            skLineSegment(sketch, "E234", {"start": v(131.53, 62.05) * mm, "end": v(142.25, 68.87) * mm});
            skLineSegment(sketch, "E235", {"start": v(131.05, 53.93) * mm, "end": v(130.06, 55.48) * mm});
            skLineSegment(sketch, "E236", {"start": v(148.34, 59.28) * mm, "end": v(137.62, 52.46) * mm});
            skLineSegment(sketch, "E237", {"start": v(156.74, 40.16) * mm, "end": v(156.74, 42) * mm});
            skLineSegment(sketch, "E238", {"start": v(159.92, 48.35) * mm, "end": v(156.74, 48.35) * mm});
            skLineSegment(sketch, "E239", {"start": v(159.92, 33.8) * mm, "end": v(156.74, 33.8) * mm});
            skLineSegment(sketch, "E240", {"start": v(149.8, 65.85) * mm, "end": v(148.82, 67.4) * mm});
            skLineSegment(sketch, "E241", {"start": v(155.9, 62.2) * mm, "end": v(155.85, 62.17) * mm});
            skLineSegment(sketch, "E242", {"start": v(155.85, 62.17) * mm, "end": v(155.53, 61.96) * mm});
            skLineSegment(sketch, "E243", {"start": v(155.53, 61.96) * mm, "end": v(154.93, 61.58) * mm});
            skLineSegment(sketch, "E244", {"start": v(154.93, 61.58) * mm, "end": v(154.13, 61.07) * mm});
            skLineSegment(sketch, "E245", {"start": v(154.13, 61.07) * mm, "end": v(153.21, 60.49) * mm});
            skLineSegment(sketch, "E246", {"start": v(145.41, 72.76) * mm, "end": v(146.33, 73.34) * mm});
            skLineSegment(sketch, "E247", {"start": v(146.33, 73.34) * mm, "end": v(147.14, 73.85) * mm});
            skLineSegment(sketch, "E248", {"start": v(147.14, 73.85) * mm, "end": v(147.73, 74.24) * mm});
            skLineSegment(sketch, "E249", {"start": v(147.73, 74.24) * mm, "end": v(148.05, 74.44) * mm});
            skLineSegment(sketch, "E250", {"start": v(148.05, 74.44) * mm, "end": v(148.1, 74.46) * mm});
            skLineSegment(sketch, "E251", {"start": v(165.22, 209.3) * mm, "end": v(170.51, 212.65) * mm});
            skLineSegment(sketch, "E252", {"start": v(249.53, 57.13) * mm, "end": v(254.81, 60.49) * mm});
            skLineSegment(sketch, "E253", {"start": v(258.34, 48.35) * mm, "end": v(252.08, 48.35) * mm});
            skLineSegment(sketch, "E254", {"start": v(174.04, 200.51) * mm, "end": v(167.78, 200.51) * mm});
            skLineSegment(sketch, "E255", {"start": v(240.88, 46.76) * mm, "end": v(253.58, 46.76) * mm});
            skLineSegment(sketch, "E256", {"start": v(236.12, 40.16) * mm, "end": v(236.12, 42) * mm});
            skLineSegment(sketch, "E257", {"start": v(253.58, 35.4) * mm, "end": v(240.88, 35.4) * mm});
            skLineSegment(sketch, "E258", {"start": v(156.58, 198.92) * mm, "end": v(169.28, 198.92) * mm});
            skLineSegment(sketch, "E259", {"start": v(220.6, 33.8) * mm, "end": v(258.34, 33.8) * mm});
            skLineSegment(sketch, "E260", {"start": v(247.01, 72.76) * mm, "end": v(215.16, 52.51) * mm});
            skLineSegment(sketch, "E261", {"start": v(151.82, 192.32) * mm, "end": v(151.82, 194.16) * mm});
            skLineSegment(sketch, "E262", {"start": v(233.13, 62.05) * mm, "end": v(243.85, 68.87) * mm});
            skLineSegment(sketch, "E263", {"start": v(232.65, 53.93) * mm, "end": v(231.66, 55.48) * mm});
            skLineSegment(sketch, "E264", {"start": v(249.94, 59.28) * mm, "end": v(239.22, 52.46) * mm});
            skLineSegment(sketch, "E265", {"start": v(258.34, 40.16) * mm, "end": v(258.34, 42) * mm});
            skLineSegment(sketch, "E266", {"start": v(261.52, 48.35) * mm, "end": v(258.34, 48.35) * mm});
            skLineSegment(sketch, "E267", {"start": v(261.52, 33.8) * mm, "end": v(258.34, 33.8) * mm});
            skLineSegment(sketch, "E268", {"start": v(251.4, 65.85) * mm, "end": v(250.42, 67.4) * mm});
            skLineSegment(sketch, "E269", {"start": v(257.5, 62.2) * mm, "end": v(257.45, 62.17) * mm});
            skLineSegment(sketch, "E270", {"start": v(257.45, 62.17) * mm, "end": v(257.13, 61.96) * mm});
            skLineSegment(sketch, "E271", {"start": v(257.13, 61.96) * mm, "end": v(256.53, 61.58) * mm});
            skLineSegment(sketch, "E272", {"start": v(256.53, 61.58) * mm, "end": v(255.73, 61.07) * mm});
            skLineSegment(sketch, "E273", {"start": v(255.73, 61.07) * mm, "end": v(254.81, 60.49) * mm});
            skLineSegment(sketch, "E274", {"start": v(247.01, 72.76) * mm, "end": v(247.93, 73.34) * mm});
            skLineSegment(sketch, "E275", {"start": v(247.93, 73.34) * mm, "end": v(248.74, 73.85) * mm});
            skLineSegment(sketch, "E276", {"start": v(248.74, 73.85) * mm, "end": v(249.33, 74.24) * mm});
            skLineSegment(sketch, "E277", {"start": v(249.33, 74.24) * mm, "end": v(249.65, 74.44) * mm});
            skLineSegment(sketch, "E278", {"start": v(249.65, 74.44) * mm, "end": v(249.7, 74.46) * mm});
            skLineSegment(sketch, "E279", {"start": v(251.83, -49.98) * mm, "end": v(251.79, -50) * mm});
            skLineSegment(sketch, "E280", {"start": v(251.79, -50) * mm, "end": v(251.44, -50.15) * mm});
            skLineSegment(sketch, "E281", {"start": v(251.44, -50.15) * mm, "end": v(250.8, -50.43) * mm});
            skLineSegment(sketch, "E282", {"start": v(250.8, -50.43) * mm, "end": v(249.92, -50.82) * mm});
            skLineSegment(sketch, "E283", {"start": v(249.92, -50.82) * mm, "end": v(248.92, -51.25) * mm});
            skLineSegment(sketch, "E284", {"start": v(169.28, 187.56) * mm, "end": v(156.58, 187.56) * mm});
            skLineSegment(sketch, "E285", {"start": v(246.25, -45.14) * mm, "end": v(245.77, -44.04) * mm});
            skLineSegment(sketch, "E286", {"start": v(136.3, 185.97) * mm, "end": v(174.04, 185.97) * mm});
            skLineSegment(sketch, "E287", {"start": v(243.1, -37.93) * mm, "end": v(244.1, -37.5) * mm});
            skLineSegment(sketch, "E288", {"start": v(244.1, -37.5) * mm, "end": v(244.97, -37.11) * mm});
            skLineSegment(sketch, "E289", {"start": v(244.97, -37.11) * mm, "end": v(245.62, -36.83) * mm});
            skLineSegment(sketch, "E290", {"start": v(245.62, -36.83) * mm, "end": v(245.97, -36.68) * mm});
            skLineSegment(sketch, "E291", {"start": v(245.97, -36.68) * mm, "end": v(246, -36.66) * mm});
            skLineSegment(sketch, "E292", {"start": v(177.2, -9.5) * mm, "end": v(182.51, -60.09) * mm});
            skLineSegment(sketch, "E293", {"start": v(162.71, 224.92) * mm, "end": v(130.86, 204.68) * mm});
            skLineSegment(sketch, "E294", {"start": v(181.9, -39.02) * mm, "end": v(179.3, -14.4) * mm});
            skLineSegment(sketch, "E295", {"start": v(187.48, -43.54) * mm, "end": v(188.67, -43.42) * mm});
            skLineSegment(sketch, "E296", {"start": v(190.6, -13.2) * mm, "end": v(193.2, -37.83) * mm});
            skLineSegment(sketch, "E297", {"start": v(148.83, 214.22) * mm, "end": v(159.54, 221.03) * mm});
            skLineSegment(sketch, "E298", {"start": v(193.77, -28.08) * mm, "end": v(191.65, -7.99) * mm});
            skLineSegment(sketch, "E299", {"start": v(220, -45.75) * mm, "end": v(196.26, -31.94) * mm});
            skLineSegment(sketch, "E300", {"start": v(216.39, -51.33) * mm, "end": v(239.08, -41.42) * mm});
            skLineSegment(sketch, "E301", {"start": v(213.77, -58.02) * mm, "end": v(214.25, -59.12) * mm});
            skLineSegment(sketch, "E302", {"start": v(243.63, -51.83) * mm, "end": v(220.94, -61.74) * mm});
            skLineSegment(sketch, "E303", {"start": v(201.35, -36.74) * mm, "end": v(213.31, -43.7) * mm});
            skLineSegment(sketch, "E304", {"start": v(197.82, -51.46) * mm, "end": v(196.6, -39.81) * mm});
            skLineSegment(sketch, "E305", {"start": v(212.99, -49.35) * mm, "end": v(202.25, -54.04) * mm});
            skLineSegment(sketch, "E306", {"start": v(243.1, -37.93) * mm, "end": v(224.59, -46.02) * mm});
            skLineSegment(sketch, "E307", {"start": v(202.31, -71.61) * mm, "end": v(248.92, -51.25) * mm});
            skLineSegment(sketch, "E308", {"start": v(191.32, -4.83) * mm, "end": v(191.33, -4.88) * mm});
            skLineSegment(sketch, "E309", {"start": v(191.33, -4.88) * mm, "end": v(191.37, -5.25) * mm});
            skLineSegment(sketch, "E310", {"start": v(191.37, -5.25) * mm, "end": v(191.44, -5.96) * mm});
            skLineSegment(sketch, "E311", {"start": v(191.44, -5.96) * mm, "end": v(191.54, -6.9) * mm});
            skLineSegment(sketch, "E312", {"start": v(191.54, -6.9) * mm, "end": v(191.65, -7.99) * mm});
            skLineSegment(sketch, "E313", {"start": v(185.02, -8.68) * mm, "end": v(183.83, -8.8) * mm});
            skLineSegment(sketch, "E314", {"start": v(177.2, -9.5) * mm, "end": v(177.08, -8.43) * mm});
            skLineSegment(sketch, "E315", {"start": v(177.08, -8.43) * mm, "end": v(176.98, -7.48) * mm});
            skLineSegment(sketch, "E316", {"start": v(176.98, -7.48) * mm, "end": v(176.9, -6.77) * mm});
            skLineSegment(sketch, "E317", {"start": v(176.9, -6.77) * mm, "end": v(176.87, -6.4) * mm});
            skLineSegment(sketch, "E318", {"start": v(176.87, -6.4) * mm, "end": v(176.86, -6.35) * mm});
            skLineSegment(sketch, "E319", {"start": v(172.7, -48.13) * mm, "end": v(172.65, -48.14) * mm});
            skLineSegment(sketch, "E320", {"start": v(172.65, -48.14) * mm, "end": v(172.3, -48.3) * mm});
            skLineSegment(sketch, "E321", {"start": v(172.3, -48.3) * mm, "end": v(171.65, -48.58) * mm});
            skLineSegment(sketch, "E322", {"start": v(171.65, -48.58) * mm, "end": v(170.78, -48.96) * mm});
            skLineSegment(sketch, "E323", {"start": v(170.78, -48.96) * mm, "end": v(169.78, -49.4) * mm});
            skLineSegment(sketch, "E324", {"start": v(148.35, 206.1) * mm, "end": v(147.36, 207.64) * mm});
            skLineSegment(sketch, "E325", {"start": v(167.11, -43.29) * mm, "end": v(166.63, -42.18) * mm});
            skLineSegment(sketch, "E326", {"start": v(165.64, 211.44) * mm, "end": v(154.92, 204.63) * mm});
            skLineSegment(sketch, "E327", {"start": v(163.96, -36.07) * mm, "end": v(164.96, -35.64) * mm});
            skLineSegment(sketch, "E328", {"start": v(164.96, -35.64) * mm, "end": v(165.83, -35.26) * mm});
            skLineSegment(sketch, "E329", {"start": v(165.83, -35.26) * mm, "end": v(166.48, -34.97) * mm});
            skLineSegment(sketch, "E330", {"start": v(166.48, -34.97) * mm, "end": v(166.83, -34.82) * mm});
            skLineSegment(sketch, "E331", {"start": v(166.83, -34.82) * mm, "end": v(166.87, -34.8) * mm});
            skLineSegment(sketch, "E332", {"start": v(98.06, -7.65) * mm, "end": v(103.37, -58.24) * mm});
            skLineSegment(sketch, "E333", {"start": v(174.04, 192.32) * mm, "end": v(174.04, 194.16) * mm});
            skLineSegment(sketch, "E334", {"start": v(102.75, -37.17) * mm, "end": v(100.17, -12.54) * mm});
            skLineSegment(sketch, "E335", {"start": v(108.34, -41.69) * mm, "end": v(109.54, -41.56) * mm});
            skLineSegment(sketch, "E336", {"start": v(111.47, -11.35) * mm, "end": v(114.06, -35.98) * mm});
            skLineSegment(sketch, "E337", {"start": v(177.22, 200.51) * mm, "end": v(174.04, 200.51) * mm});
            skLineSegment(sketch, "E338", {"start": v(114.63, -26.22) * mm, "end": v(112.52, -6.13) * mm});
            skLineSegment(sketch, "E339", {"start": v(140.86, -43.9) * mm, "end": v(117.12, -30.08) * mm});
            skLineSegment(sketch, "E340", {"start": v(137.25, -49.48) * mm, "end": v(159.94, -39.56) * mm});
            skLineSegment(sketch, "E341", {"start": v(134.63, -56.17) * mm, "end": v(135.1, -57.27) * mm});
            skLineSegment(sketch, "E342", {"start": v(164.5, -49.98) * mm, "end": v(141.8, -59.9) * mm});
            skLineSegment(sketch, "E343", {"start": v(122.21, -34.88) * mm, "end": v(134.17, -41.84) * mm});
            skLineSegment(sketch, "E344", {"start": v(118.68, -49.6) * mm, "end": v(117.46, -37.96) * mm});
            skLineSegment(sketch, "E345", {"start": v(133.85, -47.5) * mm, "end": v(123.11, -52.19) * mm});
            skLineSegment(sketch, "E346", {"start": v(163.96, -36.07) * mm, "end": v(145.45, -44.16) * mm});
            skLineSegment(sketch, "E347", {"start": v(123.17, -69.76) * mm, "end": v(169.78, -49.4) * mm});
            skLineSegment(sketch, "E348", {"start": v(112.18, -2.97) * mm, "end": v(112.19, -3.02) * mm});
            skLineSegment(sketch, "E349", {"start": v(112.19, -3.02) * mm, "end": v(112.23, -3.4) * mm});
            skLineSegment(sketch, "E350", {"start": v(112.23, -3.4) * mm, "end": v(112.3, -4.1) * mm});
            skLineSegment(sketch, "E351", {"start": v(112.3, -4.1) * mm, "end": v(112.4, -5.05) * mm});
            skLineSegment(sketch, "E352", {"start": v(112.4, -5.05) * mm, "end": v(112.52, -6.13) * mm});
            skLineSegment(sketch, "E353", {"start": v(98.06, -7.65) * mm, "end": v(97.94, -6.57) * mm});
            skLineSegment(sketch, "E354", {"start": v(97.94, -6.57) * mm, "end": v(97.84, -5.62) * mm});
            skLineSegment(sketch, "E355", {"start": v(97.84, -5.62) * mm, "end": v(97.77, -4.92) * mm});
            skLineSegment(sketch, "E356", {"start": v(97.77, -4.92) * mm, "end": v(97.73, -4.54) * mm});
            skLineSegment(sketch, "E357", {"start": v(97.73, -4.54) * mm, "end": v(97.72, -4.5) * mm});
            skLineSegment(sketch, "E358", {"start": v(105.88, -6.83) * mm, "end": v(104.69, -6.95) * mm});
            skLineSegment(sketch, "E359", {"start": v(177.22, 185.97) * mm, "end": v(174.04, 185.97) * mm});
            skLineSegment(sketch, "E360", {"start": v(120.1, 9.91) * mm, "end": v(120.1, 11.12) * mm});
            skLineSegment(sketch, "E361", {"start": v(167.1, 218.01) * mm, "end": v(166.12, 219.56) * mm});
            skLineSegment(sketch, "E362", {"start": v(120.1, 17.78) * mm, "end": v(123.28, 17.78) * mm});
            skLineSegment(sketch, "E363", {"start": v(123.28, 3.25) * mm, "end": v(120.1, 3.25) * mm});
            skLineSegment(sketch, "E364", {"start": v(83.65, 66.4) * mm, "end": v(58.22, 22.34) * mm});
            skLineSegment(sketch, "E365", {"start": v(173.2, 214.36) * mm, "end": v(173.15, 214.33) * mm});
            skLineSegment(sketch, "E366", {"start": v(70.1, 39.75) * mm, "end": v(82.48, 61.2) * mm});
            skLineSegment(sketch, "E367", {"start": v(71.96, 32.81) * mm, "end": v(73, 32.21) * mm});
            skLineSegment(sketch, "E368", {"start": v(92.33, 55.52) * mm, "end": v(79.94, 34.07) * mm});
            skLineSegment(sketch, "E369", {"start": v(173.15, 214.33) * mm, "end": v(172.83, 214.13) * mm});
            skLineSegment(sketch, "E370", {"start": v(86.32, 41.94) * mm, "end": v(96.24, 59.12) * mm});
            skLineSegment(sketch, "E371", {"start": v(95.86, 20.32) * mm, "end": v(86.32, 36.86) * mm});
            skLineSegment(sketch, "E372", {"start": v(90.26, 16.2) * mm, "end": v(115.03, 16.2) * mm});
            skLineSegment(sketch, "E373", {"start": v(85.18, 11.12) * mm, "end": v(85.18, 9.91) * mm});
            skLineSegment(sketch, "E374", {"start": v(115.03, 4.83) * mm, "end": v(90.26, 4.83) * mm});
            skLineSegment(sketch, "E375", {"start": v(87.6, 31.46) * mm, "end": v(91.83, 24.14) * mm});
            skLineSegment(sketch, "E376", {"start": v(77.87, 24.14) * mm, "end": v(82.1, 31.46) * mm});
            skLineSegment(sketch, "E377", {"start": v(89.08, 19.37) * mm, "end": v(80.62, 19.37) * mm});
            skLineSegment(sketch, "E378", {"start": v(120.1, 17.78) * mm, "end": v(100.26, 17.78) * mm});
            skLineSegment(sketch, "E379", {"start": v(69.24, 3.25) * mm, "end": v(120.1, 3.25) * mm});
            skLineSegment(sketch, "E380", {"start": v(97.83, 61.87) * mm, "end": v(97.8, 61.83) * mm});
            skLineSegment(sketch, "E381", {"start": v(97.8, 61.83) * mm, "end": v(97.62, 61.5) * mm});
            skLineSegment(sketch, "E382", {"start": v(97.62, 61.5) * mm, "end": v(97.26, 60.9) * mm});
            skLineSegment(sketch, "E383", {"start": v(97.26, 60.9) * mm, "end": v(96.78, 60.06) * mm});
            skLineSegment(sketch, "E384", {"start": v(96.78, 60.06) * mm, "end": v(96.24, 59.12) * mm});
            skLineSegment(sketch, "E385", {"start": v(83.65, 66.4) * mm, "end": v(84.2, 67.33) * mm});
            skLineSegment(sketch, "E386", {"start": v(84.2, 67.33) * mm, "end": v(84.67, 68.16) * mm});
            skLineSegment(sketch, "E387", {"start": v(84.67, 68.16) * mm, "end": v(85.02, 68.77) * mm});
            skLineSegment(sketch, "E388", {"start": v(85.02, 68.77) * mm, "end": v(85.21, 69.1) * mm});
            skLineSegment(sketch, "E389", {"start": v(85.21, 69.1) * mm, "end": v(85.24, 69.14) * mm});
            skLineSegment(sketch, "E390", {"start": v(90.47, 62.46) * mm, "end": v(89.42, 63.06) * mm});
            skLineSegment(sketch, "E391", {"start": v(224.88, 3.25) * mm, "end": v(221.7, 3.25) * mm});
            skLineSegment(sketch, "E392", {"start": v(172.83, 214.13) * mm, "end": v(172.23, 213.75) * mm});
            skLineSegment(sketch, "E393", {"start": v(221.7, 9.91) * mm, "end": v(221.7, 11.12) * mm});
            skLineSegment(sketch, "E394", {"start": v(172.23, 213.75) * mm, "end": v(171.43, 213.24) * mm});
            skLineSegment(sketch, "E395", {"start": v(221.7, 17.78) * mm, "end": v(224.88, 17.78) * mm});
            skLineSegment(sketch, "E396", {"start": v(185.25, 66.4) * mm, "end": v(159.82, 22.34) * mm});
            skLineSegment(sketch, "E397", {"start": v(171.43, 213.24) * mm, "end": v(170.51, 212.65) * mm});
            skLineSegment(sketch, "E398", {"start": v(171.7, 39.75) * mm, "end": v(184.08, 61.2) * mm});
            skLineSegment(sketch, "E399", {"start": v(173.56, 32.81) * mm, "end": v(174.6, 32.21) * mm});
            skLineSegment(sketch, "E400", {"start": v(193.93, 55.52) * mm, "end": v(181.54, 34.07) * mm});
            skLineSegment(sketch, "E401", {"start": v(162.71, 224.92) * mm, "end": v(163.63, 225.5) * mm});
            skLineSegment(sketch, "E402", {"start": v(187.92, 41.94) * mm, "end": v(197.84, 59.12) * mm});
            skLineSegment(sketch, "E403", {"start": v(197.46, 20.32) * mm, "end": v(187.92, 36.86) * mm});
            skLineSegment(sketch, "E404", {"start": v(191.86, 16.2) * mm, "end": v(216.63, 16.2) * mm});
            skLineSegment(sketch, "E405", {"start": v(186.78, 11.12) * mm, "end": v(186.78, 9.91) * mm});
            skLineSegment(sketch, "E406", {"start": v(216.63, 4.83) * mm, "end": v(191.86, 4.83) * mm});
            skLineSegment(sketch, "E407", {"start": v(189.2, 31.46) * mm, "end": v(193.43, 24.14) * mm});
            skLineSegment(sketch, "E408", {"start": v(179.47, 24.14) * mm, "end": v(183.7, 31.46) * mm});
            skLineSegment(sketch, "E409", {"start": v(190.68, 19.37) * mm, "end": v(182.22, 19.37) * mm});
            skLineSegment(sketch, "E410", {"start": v(221.7, 17.78) * mm, "end": v(201.86, 17.78) * mm});
            skLineSegment(sketch, "E411", {"start": v(170.84, 3.25) * mm, "end": v(221.7, 3.25) * mm});
            skLineSegment(sketch, "E412", {"start": v(199.43, 61.87) * mm, "end": v(199.4, 61.83) * mm});
            skLineSegment(sketch, "E413", {"start": v(199.4, 61.83) * mm, "end": v(199.22, 61.5) * mm});
            skLineSegment(sketch, "E414", {"start": v(199.22, 61.5) * mm, "end": v(198.86, 60.9) * mm});
            skLineSegment(sketch, "E415", {"start": v(198.86, 60.9) * mm, "end": v(198.38, 60.06) * mm});
            skLineSegment(sketch, "E416", {"start": v(198.38, 60.06) * mm, "end": v(197.84, 59.12) * mm});
            skLineSegment(sketch, "E417", {"start": v(192.07, 62.46) * mm, "end": v(191.02, 63.06) * mm});
            skLineSegment(sketch, "E418", {"start": v(185.25, 66.4) * mm, "end": v(185.8, 67.33) * mm});
            skLineSegment(sketch, "E419", {"start": v(185.8, 67.33) * mm, "end": v(186.27, 68.16) * mm});
            skLineSegment(sketch, "E420", {"start": v(186.27, 68.16) * mm, "end": v(186.62, 68.77) * mm});
            skLineSegment(sketch, "E421", {"start": v(186.62, 68.77) * mm, "end": v(186.81, 69.1) * mm});
            skLineSegment(sketch, "E422", {"start": v(186.81, 69.1) * mm, "end": v(186.84, 69.14) * mm});
            skLineSegment(sketch, "E423", {"start": v(37.76, -59) * mm, "end": v(37.8, -58.97) * mm});
            skLineSegment(sketch, "E424", {"start": v(37.8, -58.97) * mm, "end": v(38.02, -58.67) * mm});
            skLineSegment(sketch, "E425", {"start": v(38.02, -58.67) * mm, "end": v(38.44, -58.1) * mm});
            skLineSegment(sketch, "E426", {"start": v(38.44, -58.1) * mm, "end": v(39.02, -57.33) * mm});
            skLineSegment(sketch, "E427", {"start": v(39.02, -57.33) * mm, "end": v(39.67, -56.46) * mm});
            skLineSegment(sketch, "E428", {"start": v(163.63, 225.5) * mm, "end": v(164.43, 226.02) * mm});
            skLineSegment(sketch, "E429", {"start": v(45, -60.46) * mm, "end": v(45.97, -61.18) * mm});
            skLineSegment(sketch, "E430", {"start": v(164.43, 226.02) * mm, "end": v(165.03, 226.4) * mm});
            skLineSegment(sketch, "E431", {"start": v(51.3, -65.18) * mm, "end": v(50.65, -66.05) * mm});
            skLineSegment(sketch, "E432", {"start": v(50.65, -66.05) * mm, "end": v(50.08, -66.81) * mm});
            skLineSegment(sketch, "E433", {"start": v(50.08, -66.81) * mm, "end": v(49.66, -67.38) * mm});
            skLineSegment(sketch, "E434", {"start": v(49.66, -67.38) * mm, "end": v(49.43, -67.68) * mm});
            skLineSegment(sketch, "E435", {"start": v(49.43, -67.68) * mm, "end": v(49.4, -67.72) * mm});
            skLineSegment(sketch, "E436", {"start": v(67.92, -40.34) * mm, "end": v(53.08, -60.16) * mm});
            skLineSegment(sketch, "E437", {"start": v(66.9, -33.23) * mm, "end": v(65.94, -32.5) * mm});
            skLineSegment(sketch, "E438", {"start": v(43.98, -53.35) * mm, "end": v(58.83, -33.53) * mm});
            skLineSegment(sketch, "E439", {"start": v(45.5, -22.61) * mm, "end": v(51.92, -35.43) * mm});
            skLineSegment(sketch, "E440", {"start": v(21.32, -19.8) * mm, "end": v(40.96, -19.8) * mm});
            skLineSegment(sketch, "E441", {"start": v(165.03, 226.4) * mm, "end": v(165.35, 226.6) * mm});
            skLineSegment(sketch, "E442", {"start": v(51.17, -18.22) * mm, "end": v(26.4, -18.22) * mm});
            skLineSegment(sketch, "E443", {"start": v(56.25, -13.14) * mm, "end": v(56.25, -11.94) * mm});
            skLineSegment(sketch, "E444", {"start": v(26.4, -6.86) * mm, "end": v(51.17, -6.86) * mm});
            skLineSegment(sketch, "E445", {"start": v(165.35, 226.6) * mm, "end": v(165.4, 226.63) * mm});
            skLineSegment(sketch, "E446", {"start": v(72.18, -5.27) * mm, "end": v(21.32, -5.27) * mm});
            skLineSegment(sketch, "E447", {"start": v(51.3, -30.63) * mm, "end": v(48.97, -26) * mm});
            skLineSegment(sketch, "E448", {"start": v(60.14, -26.47) * mm, "end": v(56.67, -31.1) * mm});
            skLineSegment(sketch, "E449", {"start": v(51.81, -21.4) * mm, "end": v(57.6, -21.4) * mm});
            skLineSegment(sketch, "E450", {"start": v(51.3, -65.18) * mm, "end": v(81.8, -24.47) * mm});
            skLineSegment(sketch, "E451", {"start": v(51.44, -40.74) * mm, "end": v(39.67, -56.46) * mm});
            skLineSegment(sketch, "E452", {"start": v(18.15, -5.27) * mm, "end": v(21.32, -5.27) * mm});
            skLineSegment(sketch, "E453", {"start": v(21.32, -11.94) * mm, "end": v(21.32, -13.14) * mm});
            skLineSegment(sketch, "E454", {"start": v(21.32, -19.8) * mm, "end": v(18.15, -19.8) * mm});
            skLineSegment(sketch, "E455", {"start": v(20.34, 12.77) * mm, "end": v(20.37, 12.8) * mm});
            skLineSegment(sketch, "E456", {"start": v(20.37, 12.8) * mm, "end": v(20.6, 13.11) * mm});
            skLineSegment(sketch, "E457", {"start": v(20.6, 13.11) * mm, "end": v(21.02, 13.68) * mm});
            skLineSegment(sketch, "E458", {"start": v(21.02, 13.68) * mm, "end": v(21.59, 14.44) * mm});
            skLineSegment(sketch, "E459", {"start": v(21.59, 14.44) * mm, "end": v(22.24, 15.31) * mm});
            skLineSegment(sketch, "E460", {"start": v(254.51, 141) * mm, "end": v(259.8, 144.36) * mm});
            skLineSegment(sketch, "E461", {"start": v(27.58, 11.32) * mm, "end": v(28.54, 10.6) * mm});
            skLineSegment(sketch, "E462", {"start": v(263.33, 132.21) * mm, "end": v(257.07, 132.21) * mm});
            skLineSegment(sketch, "E463", {"start": v(33.88, 6.6) * mm, "end": v(33.23, 5.73) * mm});
            skLineSegment(sketch, "E464", {"start": v(33.23, 5.73) * mm, "end": v(32.65, 4.96) * mm});
            skLineSegment(sketch, "E465", {"start": v(32.65, 4.96) * mm, "end": v(32.23, 4.4) * mm});
            skLineSegment(sketch, "E466", {"start": v(32.23, 4.4) * mm, "end": v(32, 4.1) * mm});
            skLineSegment(sketch, "E467", {"start": v(32, 4.1) * mm, "end": v(31.97, 4.06) * mm});
            skLineSegment(sketch, "E468", {"start": v(50.5, 31.44) * mm, "end": v(35.65, 11.62) * mm});
            skLineSegment(sketch, "E469", {"start": v(49.48, 38.55) * mm, "end": v(48.51, 39.27) * mm});
            skLineSegment(sketch, "E470", {"start": v(26.56, 18.43) * mm, "end": v(41.4, 38.25) * mm});
            skLineSegment(sketch, "E471", {"start": v(28.08, 49.16) * mm, "end": v(34.49, 36.35) * mm});
            skLineSegment(sketch, "E472", {"start": v(3.9, 51.97) * mm, "end": v(23.54, 51.97) * mm});
            skLineSegment(sketch, "E473", {"start": v(245.87, 130.63) * mm, "end": v(258.57, 130.63) * mm});
            skLineSegment(sketch, "E474", {"start": v(33.74, 53.56) * mm, "end": v(8.97, 53.56) * mm});
            skLineSegment(sketch, "E475", {"start": v(38.82, 58.64) * mm, "end": v(38.82, 59.84) * mm});
            skLineSegment(sketch, "E476", {"start": v(8.97, 64.92) * mm, "end": v(33.74, 64.92) * mm});
            skLineSegment(sketch, "E477", {"start": v(241.1, 124.02) * mm, "end": v(241.1, 125.86) * mm});
            skLineSegment(sketch, "E478", {"start": v(54.76, 66.5) * mm, "end": v(3.9, 66.5) * mm});
            skLineSegment(sketch, "E479", {"start": v(33.86, 41.15) * mm, "end": v(31.54, 45.79) * mm});
            skLineSegment(sketch, "E480", {"start": v(42.72, 45.3) * mm, "end": v(39.24, 40.67) * mm});
            skLineSegment(sketch, "E481", {"start": v(34.38, 50.38) * mm, "end": v(40.17, 50.38) * mm});
            skLineSegment(sketch, "E482", {"start": v(33.88, 6.6) * mm, "end": v(64.37, 47.3) * mm});
            skLineSegment(sketch, "E483", {"start": v(34.01, 31.03) * mm, "end": v(22.24, 15.31) * mm});
            skLineSegment(sketch, "E484", {"start": v(0.72, 66.5) * mm, "end": v(3.9, 66.5) * mm});
            skLineSegment(sketch, "E485", {"start": v(3.9, 59.84) * mm, "end": v(3.9, 58.64) * mm});
            skLineSegment(sketch, "E486", {"start": v(3.9, 51.97) * mm, "end": v(0.72, 51.97) * mm});
            skLineSegment(sketch, "E487", {"start": v(-32.73, 61.4) * mm, "end": v(-32.73, 10.53) * mm});
            skLineSegment(sketch, "E488", {"start": v(258.57, 119.26) * mm, "end": v(245.87, 119.26) * mm});
            skLineSegment(sketch, "E489", {"start": v(-31.15, 37.9) * mm, "end": v(-31.15, 56.31) * mm});
            skLineSegment(sketch, "E490", {"start": v(-26.07, 32.82) * mm, "end": v(-24.86, 32.82) * mm});
            skLineSegment(sketch, "E491", {"start": v(-19.78, 56.31) * mm, "end": v(-19.78, 37.9) * mm});
            skLineSegment(sketch, "E492", {"start": v(225.59, 117.67) * mm, "end": v(263.33, 117.67) * mm});
            skLineSegment(sketch, "E493", {"start": v(-18.2, 41.93) * mm, "end": v(-18.2, 61.4) * mm});
            skLineSegment(sketch, "E494", {"start": v(-5.84, 33.2) * mm, "end": v(-15.15, 37.28) * mm});
            skLineSegment(sketch, "E495", {"start": v(13.94, 47.32) * mm, "end": v(-0.36, 34.12) * mm});
            skLineSegment(sketch, "E496", {"start": v(252, 156.63) * mm, "end": v(220.15, 136.38) * mm});
            skLineSegment(sketch, "E497", {"start": v(-2.25, 30.22) * mm, "end": v(11.28, 42.7) * mm});
            skLineSegment(sketch, "E498", {"start": v(-2.54, 23.04) * mm, "end": v(-1.72, 22.16) * mm});
            skLineSegment(sketch, "E499", {"start": v(18.99, 34.36) * mm, "end": v(5.46, 21.87) * mm});
            skLineSegment(sketch, "E500", {"start": v(238.11, 145.92) * mm, "end": v(248.83, 152.73) * mm});
            skLineSegment(sketch, "E501", {"start": v(-13.58, 2.14) * mm, "end": v(23.8, 36.63) * mm});
            skLineSegment(sketch, "E502", {"start": v(-32.73, 61.4) * mm, "end": v(-32.73, 64.57) * mm});
            skLineSegment(sketch, "E503", {"start": v(-18.2, 64.57) * mm, "end": v(-18.2, 61.4) * mm});
            skLineSegment(sketch, "E504", {"start": v(-24.86, 61.4) * mm, "end": v(-26.07, 61.4) * mm});
            skLineSegment(sketch, "E505", {"start": v(19.28, 41.53) * mm, "end": v(18.46, 42.42) * mm});
            skLineSegment(sketch, "E506", {"start": v(13.94, 47.32) * mm, "end": v(14.74, 48.05) * mm});
            skLineSegment(sketch, "E507", {"start": v(14.74, 48.05) * mm, "end": v(15.44, 48.7) * mm});
            skLineSegment(sketch, "E508", {"start": v(15.44, 48.7) * mm, "end": v(15.96, 49.18) * mm});
            skLineSegment(sketch, "E509", {"start": v(15.96, 49.18) * mm, "end": v(16.24, 49.44) * mm});
            skLineSegment(sketch, "E510", {"start": v(16.24, 49.44) * mm, "end": v(16.27, 49.47) * mm});
            skLineSegment(sketch, "E511", {"start": v(26.13, 38.79) * mm, "end": v(26.1, 38.75) * mm});
            skLineSegment(sketch, "E512", {"start": v(26.1, 38.75) * mm, "end": v(25.82, 38.5) * mm});
            skLineSegment(sketch, "E513", {"start": v(25.82, 38.5) * mm, "end": v(25.3, 38.02) * mm});
            skLineSegment(sketch, "E514", {"start": v(25.3, 38.02) * mm, "end": v(24.6, 37.37) * mm});
            skLineSegment(sketch, "E515", {"start": v(24.6, 37.37) * mm, "end": v(23.8, 36.63) * mm});
            skLineSegment(sketch, "E516", {"start": v(-15.3, -10.39) * mm, "end": v(-15.3, -61.25) * mm});
            skLineSegment(sketch, "E517", {"start": v(237.63, 137.8) * mm, "end": v(236.65, 139.34) * mm});
            skLineSegment(sketch, "E518", {"start": v(-13.72, -33.88) * mm, "end": v(-13.72, -15.47) * mm});
            skLineSegment(sketch, "E519", {"start": v(-8.64, -38.96) * mm, "end": v(-7.44, -38.96) * mm});
            skLineSegment(sketch, "E520", {"start": v(-2.36, -15.47) * mm, "end": v(-2.36, -33.88) * mm});
            skLineSegment(sketch, "E521", {"start": v(254.93, 143.14) * mm, "end": v(244.2, 136.33) * mm});
            skLineSegment(sketch, "E522", {"start": v(-0.77, -29.84) * mm, "end": v(-0.77, -10.39) * mm});
            skLineSegment(sketch, "E523", {"start": v(11.58, -38.57) * mm, "end": v(2.27, -34.5) * mm});
            skLineSegment(sketch, "E524", {"start": v(31.37, -24.46) * mm, "end": v(17.07, -37.65) * mm});
            skLineSegment(sketch, "E525", {"start": v(263.33, 124.02) * mm, "end": v(263.33, 125.86) * mm});
            skLineSegment(sketch, "E526", {"start": v(15.18, -41.56) * mm, "end": v(28.7, -29.07) * mm});
            skLineSegment(sketch, "E527", {"start": v(14.89, -48.74) * mm, "end": v(15.7, -49.62) * mm});
            skLineSegment(sketch, "E528", {"start": v(36.42, -37.42) * mm, "end": v(22.88, -49.91) * mm});
            skLineSegment(sketch, "E529", {"start": v(266.5, 132.21) * mm, "end": v(263.33, 132.21) * mm});
            skLineSegment(sketch, "E530", {"start": v(3.85, -69.64) * mm, "end": v(41.23, -35.14) * mm});
            skLineSegment(sketch, "E531", {"start": v(-7.44, -10.39) * mm, "end": v(-8.64, -10.39) * mm});
            skLineSegment(sketch, "E532", {"start": v(-15.3, -10.39) * mm, "end": v(-15.3, -7.21) * mm});
            skLineSegment(sketch, "E533", {"start": v(-0.77, -7.21) * mm, "end": v(-0.77, -10.39) * mm});
            skLineSegment(sketch, "E534", {"start": v(36.7, -30.24) * mm, "end": v(35.89, -29.36) * mm});
            skLineSegment(sketch, "E535", {"start": v(31.37, -24.46) * mm, "end": v(32.16, -23.72) * mm});
            skLineSegment(sketch, "E536", {"start": v(32.16, -23.72) * mm, "end": v(32.87, -23.07) * mm});
            skLineSegment(sketch, "E537", {"start": v(32.87, -23.07) * mm, "end": v(33.39, -22.6) * mm});
            skLineSegment(sketch, "E538", {"start": v(33.39, -22.6) * mm, "end": v(33.66, -22.34) * mm});
            skLineSegment(sketch, "E539", {"start": v(33.66, -22.34) * mm, "end": v(33.7, -22.3) * mm});
            skLineSegment(sketch, "E540", {"start": v(43.56, -33) * mm, "end": v(43.52, -33.02) * mm});
            skLineSegment(sketch, "E541", {"start": v(43.52, -33.02) * mm, "end": v(43.25, -33.28) * mm});
            skLineSegment(sketch, "E542", {"start": v(43.25, -33.28) * mm, "end": v(42.73, -33.76) * mm});
            skLineSegment(sketch, "E543", {"start": v(42.73, -33.76) * mm, "end": v(42.02, -34.4) * mm});
            skLineSegment(sketch, "E544", {"start": v(42.02, -34.4) * mm, "end": v(41.23, -35.14) * mm});
            skLineSegment(sketch, "E545", {"start": v(266.5, 117.67) * mm, "end": v(263.33, 117.67) * mm});
            skLineSegment(sketch, "E546", {"start": v(256.4, 149.71) * mm, "end": v(255.4, 151.27) * mm});
            skLineSegment(sketch, "E547", {"start": v(262.48, 146.06) * mm, "end": v(262.44, 146.03) * mm});
            skLineSegment(sketch, "E548", {"start": v(262.44, 146.03) * mm, "end": v(262.12, 145.83) * mm});
            skLineSegment(sketch, "E549", {"start": v(262.12, 145.83) * mm, "end": v(261.52, 145.45) * mm});
            skLineSegment(sketch, "E550", {"start": v(261.52, 145.45) * mm, "end": v(260.71, 144.94) * mm});
            skLineSegment(sketch, "E551", {"start": v(260.71, 144.94) * mm, "end": v(259.8, 144.36) * mm});
            skLineSegment(sketch, "E552", {"start": v(252, 156.63) * mm, "end": v(252.92, 157.2) * mm});
            skLineSegment(sketch, "E553", {"start": v(252.92, 157.2) * mm, "end": v(253.72, 157.72) * mm});
            skLineSegment(sketch, "E554", {"start": v(253.72, 157.72) * mm, "end": v(254.32, 158.1) * mm});
            skLineSegment(sketch, "E555", {"start": v(254.32, 158.1) * mm, "end": v(254.64, 158.3) * mm});
            skLineSegment(sketch, "E556", {"start": v(254.64, 158.3) * mm, "end": v(254.68, 158.33) * mm});
            skLineSegment(sketch, "E557", {"start": v(236.2, 98.34) * mm, "end": v(236.15, 98.32) * mm});
            skLineSegment(sketch, "E558", {"start": v(236.15, 98.32) * mm, "end": v(235.8, 98.17) * mm});
            skLineSegment(sketch, "E559", {"start": v(235.8, 98.17) * mm, "end": v(235.16, 97.88) * mm});
            skLineSegment(sketch, "E560", {"start": v(235.16, 97.88) * mm, "end": v(234.28, 97.5) * mm});
            skLineSegment(sketch, "E561", {"start": v(234.28, 97.5) * mm, "end": v(233.29, 97.07) * mm});
            skLineSegment(sketch, "E562", {"start": v(230.62, 103.18) * mm, "end": v(230.14, 104.28) * mm});
            skLineSegment(sketch, "E563", {"start": v(227.47, 110.39) * mm, "end": v(228.46, 110.82) * mm});
            skLineSegment(sketch, "E564", {"start": v(228.46, 110.82) * mm, "end": v(229.34, 111.2) * mm});
            skLineSegment(sketch, "E565", {"start": v(229.34, 111.2) * mm, "end": v(229.99, 111.49) * mm});
            skLineSegment(sketch, "E566", {"start": v(229.99, 111.49) * mm, "end": v(230.33, 111.64) * mm});
            skLineSegment(sketch, "E567", {"start": v(230.33, 111.64) * mm, "end": v(230.38, 111.66) * mm});
            skLineSegment(sketch, "E568", {"start": v(161.56, 138.81) * mm, "end": v(166.88, 88.23) * mm});
            skLineSegment(sketch, "E569", {"start": v(166.26, 109.3) * mm, "end": v(163.67, 133.92) * mm});
            skLineSegment(sketch, "E570", {"start": v(171.84, 104.77) * mm, "end": v(173.04, 104.9) * mm});
            skLineSegment(sketch, "E571", {"start": v(174.97, 135.11) * mm, "end": v(177.56, 110.48) * mm});
            skLineSegment(sketch, "E572", {"start": v(178.13, 120.24) * mm, "end": v(176.02, 140.33) * mm});
            skLineSegment(sketch, "E573", {"start": v(204.37, 102.57) * mm, "end": v(180.63, 116.38) * mm});
            skLineSegment(sketch, "E574", {"start": v(200.75, 96.99) * mm, "end": v(223.45, 106.9) * mm});
            skLineSegment(sketch, "E575", {"start": v(198.13, 90.3) * mm, "end": v(198.61, 89.2) * mm});
            skLineSegment(sketch, "E576", {"start": v(228, 96.49) * mm, "end": v(205.3, 86.57) * mm});
            skLineSegment(sketch, "E577", {"start": v(185.72, 111.58) * mm, "end": v(197.68, 104.62) * mm});
            skLineSegment(sketch, "E578", {"start": v(182.19, 96.85) * mm, "end": v(180.96, 108.5) * mm});
            skLineSegment(sketch, "E579", {"start": v(197.35, 98.97) * mm, "end": v(186.62, 94.28) * mm});
            skLineSegment(sketch, "E580", {"start": v(227.47, 110.39) * mm, "end": v(208.95, 102.3) * mm});
            skLineSegment(sketch, "E581", {"start": v(186.68, 76.7) * mm, "end": v(233.29, 97.07) * mm});
            skLineSegment(sketch, "E582", {"start": v(175.69, 143.49) * mm, "end": v(175.7, 143.44) * mm});
            skLineSegment(sketch, "E583", {"start": v(175.7, 143.44) * mm, "end": v(175.73, 143.07) * mm});
            skLineSegment(sketch, "E584", {"start": v(175.73, 143.07) * mm, "end": v(175.8, 142.36) * mm});
            skLineSegment(sketch, "E585", {"start": v(175.8, 142.36) * mm, "end": v(175.9, 141.41) * mm});
            skLineSegment(sketch, "E586", {"start": v(175.9, 141.41) * mm, "end": v(176.02, 140.33) * mm});
            skLineSegment(sketch, "E587", {"start": v(169.4, 139.63) * mm, "end": v(168.2, 139.5) * mm});
            skLineSegment(sketch, "E588", {"start": v(161.56, 138.81) * mm, "end": v(161.45, 139.9) * mm});
            skLineSegment(sketch, "E589", {"start": v(161.45, 139.9) * mm, "end": v(161.35, 140.84) * mm});
            skLineSegment(sketch, "E590", {"start": v(161.35, 140.84) * mm, "end": v(161.28, 141.55) * mm});
            skLineSegment(sketch, "E591", {"start": v(161.28, 141.55) * mm, "end": v(161.24, 141.92) * mm});
            skLineSegment(sketch, "E592", {"start": v(161.24, 141.92) * mm, "end": v(161.23, 141.97) * mm});
            skLineSegment(sketch, "E593", {"start": v(157.06, 100.2) * mm, "end": v(157.01, 100.17) * mm});
            skLineSegment(sketch, "E594", {"start": v(157.01, 100.17) * mm, "end": v(156.67, 100.02) * mm});
            skLineSegment(sketch, "E595", {"start": v(156.67, 100.02) * mm, "end": v(156.02, 99.74) * mm});
            skLineSegment(sketch, "E596", {"start": v(156.02, 99.74) * mm, "end": v(155.14, 99.35) * mm});
            skLineSegment(sketch, "E597", {"start": v(155.14, 99.35) * mm, "end": v(154.15, 98.92) * mm});
            skLineSegment(sketch, "E598", {"start": v(151.48, 105.03) * mm, "end": v(151, 106.13) * mm});
            skLineSegment(sketch, "E599", {"start": v(148.33, 112.24) * mm, "end": v(149.32, 112.68) * mm});
            skLineSegment(sketch, "E600", {"start": v(149.32, 112.68) * mm, "end": v(150.2, 113.06) * mm});
            skLineSegment(sketch, "E601", {"start": v(150.2, 113.06) * mm, "end": v(150.85, 113.34) * mm});
            skLineSegment(sketch, "E602", {"start": v(150.85, 113.34) * mm, "end": v(151.2, 113.5) * mm});
            skLineSegment(sketch, "E603", {"start": v(151.2, 113.5) * mm, "end": v(151.24, 113.51) * mm});
            skLineSegment(sketch, "E604", {"start": v(82.42, 140.66) * mm, "end": v(87.74, 90.08) * mm});
            skLineSegment(sketch, "E605", {"start": v(87.12, 111.15) * mm, "end": v(84.53, 135.78) * mm});
            skLineSegment(sketch, "E606", {"start": v(92.7, 106.63) * mm, "end": v(93.9, 106.75) * mm});
            skLineSegment(sketch, "E607", {"start": v(95.83, 136.97) * mm, "end": v(98.42, 112.34) * mm});
            skLineSegment(sketch, "E608", {"start": v(99, 122.1) * mm, "end": v(96.88, 142.18) * mm});
            skLineSegment(sketch, "E609", {"start": v(125.23, 104.42) * mm, "end": v(101.5, 118.23) * mm});
            skLineSegment(sketch, "E610", {"start": v(121.61, 98.84) * mm, "end": v(144.3, 108.75) * mm});
            skLineSegment(sketch, "E611", {"start": v(119, 92.15) * mm, "end": v(119.47, 91.05) * mm});
            skLineSegment(sketch, "E612", {"start": v(148.86, 98.34) * mm, "end": v(126.16, 88.43) * mm});
            skLineSegment(sketch, "E613", {"start": v(106.58, 113.44) * mm, "end": v(118.54, 106.47) * mm});
            skLineSegment(sketch, "E614", {"start": v(103.05, 98.7) * mm, "end": v(101.82, 110.36) * mm});
            skLineSegment(sketch, "E615", {"start": v(118.21, 100.82) * mm, "end": v(107.48, 96.13) * mm});
            skLineSegment(sketch, "E616", {"start": v(148.33, 112.24) * mm, "end": v(129.82, 104.15) * mm});
            skLineSegment(sketch, "E617", {"start": v(107.54, 78.56) * mm, "end": v(154.15, 98.92) * mm});
            skLineSegment(sketch, "E618", {"start": v(96.55, 145.34) * mm, "end": v(96.56, 145.3) * mm});
            skLineSegment(sketch, "E619", {"start": v(96.56, 145.3) * mm, "end": v(96.6, 144.92) * mm});
            skLineSegment(sketch, "E620", {"start": v(96.6, 144.92) * mm, "end": v(96.67, 144.21) * mm});
            skLineSegment(sketch, "E621", {"start": v(96.67, 144.21) * mm, "end": v(96.77, 143.26) * mm});
            skLineSegment(sketch, "E622", {"start": v(96.77, 143.26) * mm, "end": v(96.88, 142.18) * mm});
            skLineSegment(sketch, "E623", {"start": v(82.42, 140.66) * mm, "end": v(82.3, 141.74) * mm});
            skLineSegment(sketch, "E624", {"start": v(82.3, 141.74) * mm, "end": v(82.2, 142.7) * mm});
            skLineSegment(sketch, "E625", {"start": v(82.2, 142.7) * mm, "end": v(82.14, 143.4) * mm});
            skLineSegment(sketch, "E626", {"start": v(82.14, 143.4) * mm, "end": v(82.1, 143.77) * mm});
            skLineSegment(sketch, "E627", {"start": v(82.1, 143.77) * mm, "end": v(82.1, 143.82) * mm});
            skLineSegment(sketch, "E628", {"start": v(90.25, 141.49) * mm, "end": v(89.05, 141.36) * mm});
            skLineSegment(sketch, "E629", {"start": v(137.4, 162.08) * mm, "end": v(137.4, 163.28) * mm});
            skLineSegment(sketch, "E630", {"start": v(137.4, 169.95) * mm, "end": v(140.58, 169.95) * mm});
            skLineSegment(sketch, "E631", {"start": v(140.58, 155.4) * mm, "end": v(137.4, 155.4) * mm});
            skLineSegment(sketch, "E632", {"start": v(100.95, 218.56) * mm, "end": v(75.52, 174.5) * mm});
            skLineSegment(sketch, "E633", {"start": v(87.4, 191.92) * mm, "end": v(99.78, 213.36) * mm});
            skLineSegment(sketch, "E634", {"start": v(89.26, 184.98) * mm, "end": v(90.3, 184.38) * mm});
            skLineSegment(sketch, "E635", {"start": v(109.62, 207.68) * mm, "end": v(97.24, 186.23) * mm});
            skLineSegment(sketch, "E636", {"start": v(103.62, 194.1) * mm, "end": v(113.54, 211.29) * mm});
            skLineSegment(sketch, "E637", {"start": v(113.16, 172.49) * mm, "end": v(103.62, 189.02) * mm});
            skLineSegment(sketch, "E638", {"start": v(107.56, 168.36) * mm, "end": v(132.33, 168.36) * mm});
            skLineSegment(sketch, "E639", {"start": v(102.48, 163.28) * mm, "end": v(102.48, 162.08) * mm});
            skLineSegment(sketch, "E640", {"start": v(132.33, 157) * mm, "end": v(107.56, 157) * mm});
            skLineSegment(sketch, "E641", {"start": v(104.9, 183.62) * mm, "end": v(109.13, 176.3) * mm});
            skLineSegment(sketch, "E642", {"start": v(95.17, 176.3) * mm, "end": v(99.4, 183.62) * mm});
            skLineSegment(sketch, "E643", {"start": v(106.38, 171.54) * mm, "end": v(97.92, 171.54) * mm});
            skLineSegment(sketch, "E644", {"start": v(137.4, 169.95) * mm, "end": v(117.56, 169.95) * mm});
            skLineSegment(sketch, "E645", {"start": v(86.54, 155.4) * mm, "end": v(137.4, 155.4) * mm});
            skLineSegment(sketch, "E646", {"start": v(115.13, 214.04) * mm, "end": v(115.1, 214) * mm});
            skLineSegment(sketch, "E647", {"start": v(115.1, 214) * mm, "end": v(114.91, 213.67) * mm});
            skLineSegment(sketch, "E648", {"start": v(114.91, 213.67) * mm, "end": v(114.56, 213.05) * mm});
            skLineSegment(sketch, "E649", {"start": v(114.56, 213.05) * mm, "end": v(114.08, 212.23) * mm});
            skLineSegment(sketch, "E650", {"start": v(114.08, 212.23) * mm, "end": v(113.54, 211.29) * mm});
            skLineSegment(sketch, "E651", {"start": v(100.95, 218.56) * mm, "end": v(101.5, 219.5) * mm});
            skLineSegment(sketch, "E652", {"start": v(101.5, 219.5) * mm, "end": v(101.97, 220.32) * mm});
            skLineSegment(sketch, "E653", {"start": v(101.97, 220.32) * mm, "end": v(102.32, 220.94) * mm});
            skLineSegment(sketch, "E654", {"start": v(102.32, 220.94) * mm, "end": v(102.51, 221.26) * mm});
            skLineSegment(sketch, "E655", {"start": v(102.51, 221.26) * mm, "end": v(102.54, 221.3) * mm});
            skLineSegment(sketch, "E656", {"start": v(107.76, 214.62) * mm, "end": v(106.72, 215.22) * mm});
            skLineSegment(sketch, "E657", {"start": v(242.18, 155.4) * mm, "end": v(239, 155.4) * mm});
            skLineSegment(sketch, "E658", {"start": v(239, 162.08) * mm, "end": v(239, 163.28) * mm});
            skLineSegment(sketch, "E659", {"start": v(239, 169.95) * mm, "end": v(242.18, 169.95) * mm});
            skLineSegment(sketch, "E660", {"start": v(202.55, 218.56) * mm, "end": v(177.12, 174.5) * mm});
            skLineSegment(sketch, "E661", {"start": v(189, 191.92) * mm, "end": v(201.38, 213.36) * mm});
            skLineSegment(sketch, "E662", {"start": v(190.86, 184.98) * mm, "end": v(191.9, 184.38) * mm});
            skLineSegment(sketch, "E663", {"start": v(211.22, 207.68) * mm, "end": v(198.84, 186.23) * mm});
            skLineSegment(sketch, "E664", {"start": v(205.22, 194.1) * mm, "end": v(215.14, 211.29) * mm});
            skLineSegment(sketch, "E665", {"start": v(214.76, 172.49) * mm, "end": v(205.22, 189.02) * mm});
            skLineSegment(sketch, "E666", {"start": v(209.16, 168.36) * mm, "end": v(233.93, 168.36) * mm});
            skLineSegment(sketch, "E667", {"start": v(204.08, 163.28) * mm, "end": v(204.08, 162.08) * mm});
            skLineSegment(sketch, "E668", {"start": v(233.93, 157) * mm, "end": v(209.16, 157) * mm});
            skLineSegment(sketch, "E669", {"start": v(206.5, 183.62) * mm, "end": v(210.73, 176.3) * mm});
            skLineSegment(sketch, "E670", {"start": v(196.77, 176.3) * mm, "end": v(201, 183.62) * mm});
            skLineSegment(sketch, "E671", {"start": v(207.98, 171.54) * mm, "end": v(199.52, 171.54) * mm});
            skLineSegment(sketch, "E672", {"start": v(239, 169.95) * mm, "end": v(219.16, 169.95) * mm});
            skLineSegment(sketch, "E673", {"start": v(188.14, 155.4) * mm, "end": v(239, 155.4) * mm});
            skLineSegment(sketch, "E674", {"start": v(216.73, 214.04) * mm, "end": v(216.7, 214) * mm});
            skLineSegment(sketch, "E675", {"start": v(216.7, 214) * mm, "end": v(216.51, 213.67) * mm});
            skLineSegment(sketch, "E676", {"start": v(216.51, 213.67) * mm, "end": v(216.16, 213.05) * mm});
            skLineSegment(sketch, "E677", {"start": v(216.16, 213.05) * mm, "end": v(215.68, 212.23) * mm});
            skLineSegment(sketch, "E678", {"start": v(215.68, 212.23) * mm, "end": v(215.14, 211.29) * mm});
            skLineSegment(sketch, "E679", {"start": v(209.36, 214.62) * mm, "end": v(208.32, 215.22) * mm});
            skLineSegment(sketch, "E680", {"start": v(202.55, 218.56) * mm, "end": v(203.1, 219.5) * mm});
            skLineSegment(sketch, "E681", {"start": v(203.1, 219.5) * mm, "end": v(203.57, 220.32) * mm});
            skLineSegment(sketch, "E682", {"start": v(203.57, 220.32) * mm, "end": v(203.92, 220.94) * mm});
            skLineSegment(sketch, "E683", {"start": v(203.92, 220.94) * mm, "end": v(204.11, 221.26) * mm});
            skLineSegment(sketch, "E684", {"start": v(204.11, 221.26) * mm, "end": v(204.14, 221.3) * mm});
            skLineSegment(sketch, "E685", {"start": v(22.13, 89.31) * mm, "end": v(22.16, 89.35) * mm});
            skLineSegment(sketch, "E686", {"start": v(22.16, 89.35) * mm, "end": v(22.38, 89.65) * mm});
            skLineSegment(sketch, "E687", {"start": v(22.38, 89.65) * mm, "end": v(22.8, 90.22) * mm});
            skLineSegment(sketch, "E688", {"start": v(22.8, 90.22) * mm, "end": v(23.38, 90.98) * mm});
            skLineSegment(sketch, "E689", {"start": v(23.38, 90.98) * mm, "end": v(24.03, 91.85) * mm});
            skLineSegment(sketch, "E690", {"start": v(29.37, 87.85) * mm, "end": v(30.33, 87.13) * mm});
            skLineSegment(sketch, "E691", {"start": v(35.67, 83.14) * mm, "end": v(35.02, 82.27) * mm});
            skLineSegment(sketch, "E692", {"start": v(35.02, 82.27) * mm, "end": v(34.45, 81.5) * mm});
            skLineSegment(sketch, "E693", {"start": v(34.45, 81.5) * mm, "end": v(34.02, 80.94) * mm});
            skLineSegment(sketch, "E694", {"start": v(34.02, 80.94) * mm, "end": v(33.8, 80.63) * mm});
            skLineSegment(sketch, "E695", {"start": v(33.8, 80.63) * mm, "end": v(33.77, 80.6) * mm});
            skLineSegment(sketch, "E696", {"start": v(52.3, 107.98) * mm, "end": v(37.44, 88.15) * mm});
            skLineSegment(sketch, "E697", {"start": v(51.27, 115.09) * mm, "end": v(50.3, 115.8) * mm});
            skLineSegment(sketch, "E698", {"start": v(28.35, 94.97) * mm, "end": v(43.2, 114.79) * mm});
            skLineSegment(sketch, "E699", {"start": v(29.87, 125.7) * mm, "end": v(36.28, 112.9) * mm});
            skLineSegment(sketch, "E700", {"start": v(5.69, 128.5) * mm, "end": v(25.33, 128.5) * mm});
            skLineSegment(sketch, "E701", {"start": v(35.53, 130.1) * mm, "end": v(10.77, 130.1) * mm});
            skLineSegment(sketch, "E702", {"start": v(40.61, 135.18) * mm, "end": v(40.61, 136.38) * mm});
            skLineSegment(sketch, "E703", {"start": v(10.77, 141.46) * mm, "end": v(35.53, 141.46) * mm});
            skLineSegment(sketch, "E704", {"start": v(56.55, 143.05) * mm, "end": v(5.69, 143.05) * mm});
            skLineSegment(sketch, "E705", {"start": v(35.66, 117.69) * mm, "end": v(33.34, 122.32) * mm});
            skLineSegment(sketch, "E706", {"start": v(44.5, 121.84) * mm, "end": v(41.04, 117.2) * mm});
            skLineSegment(sketch, "E707", {"start": v(36.18, 126.92) * mm, "end": v(41.97, 126.92) * mm});
            skLineSegment(sketch, "E708", {"start": v(35.67, 83.14) * mm, "end": v(66.16, 123.85) * mm});
            skLineSegment(sketch, "E709", {"start": v(35.8, 107.57) * mm, "end": v(24.03, 91.85) * mm});
            skLineSegment(sketch, "E710", {"start": v(2.51, 143.05) * mm, "end": v(5.69, 143.05) * mm});
            skLineSegment(sketch, "E711", {"start": v(5.69, 136.38) * mm, "end": v(5.69, 135.18) * mm});
            skLineSegment(sketch, "E712", {"start": v(5.69, 128.5) * mm, "end": v(2.51, 128.5) * mm});
            skLineSegment(sketch, "E713", {"start": v(37.63, 164.94) * mm, "end": v(37.66, 164.97) * mm});
            skLineSegment(sketch, "E714", {"start": v(37.66, 164.97) * mm, "end": v(37.89, 165.28) * mm});
            skLineSegment(sketch, "E715", {"start": v(37.89, 165.28) * mm, "end": v(38.31, 165.84) * mm});
            skLineSegment(sketch, "E716", {"start": v(38.31, 165.84) * mm, "end": v(38.89, 166.6) * mm});
            skLineSegment(sketch, "E717", {"start": v(38.89, 166.6) * mm, "end": v(39.54, 167.48) * mm});
            skLineSegment(sketch, "E718", {"start": v(44.87, 163.48) * mm, "end": v(45.84, 162.76) * mm});
            skLineSegment(sketch, "E719", {"start": v(51.18, 158.76) * mm, "end": v(50.52, 157.9) * mm});
            skLineSegment(sketch, "E720", {"start": v(50.52, 157.9) * mm, "end": v(49.95, 157.13) * mm});
            skLineSegment(sketch, "E721", {"start": v(49.95, 157.13) * mm, "end": v(49.53, 156.56) * mm});
            skLineSegment(sketch, "E722", {"start": v(49.53, 156.56) * mm, "end": v(49.3, 156.26) * mm});
            skLineSegment(sketch, "E723", {"start": v(49.3, 156.26) * mm, "end": v(49.27, 156.22) * mm});
            skLineSegment(sketch, "E724", {"start": v(67.8, 183.6) * mm, "end": v(52.95, 163.78) * mm});
            skLineSegment(sketch, "E725", {"start": v(66.77, 190.71) * mm, "end": v(65.81, 191.43) * mm});
            skLineSegment(sketch, "E726", {"start": v(43.85, 170.6) * mm, "end": v(58.7, 190.41) * mm});
            skLineSegment(sketch, "E727", {"start": v(45.38, 201.33) * mm, "end": v(51.79, 188.52) * mm});
            skLineSegment(sketch, "E728", {"start": v(21.2, 204.13) * mm, "end": v(40.83, 204.13) * mm});
            skLineSegment(sketch, "E729", {"start": v(51.04, 205.72) * mm, "end": v(26.27, 205.72) * mm});
            skLineSegment(sketch, "E730", {"start": v(56.12, 210.8) * mm, "end": v(56.12, 212) * mm});
            skLineSegment(sketch, "E731", {"start": v(26.27, 217.09) * mm, "end": v(51.04, 217.09) * mm});
            skLineSegment(sketch, "E732", {"start": v(72.06, 218.67) * mm, "end": v(21.2, 218.67) * mm});
            skLineSegment(sketch, "E733", {"start": v(51.16, 193.31) * mm, "end": v(48.84, 197.95) * mm});
            skLineSegment(sketch, "E734", {"start": v(60.01, 197.47) * mm, "end": v(56.54, 192.83) * mm});
            skLineSegment(sketch, "E735", {"start": v(51.68, 202.55) * mm, "end": v(57.47, 202.55) * mm});
            skLineSegment(sketch, "E736", {"start": v(51.18, 158.76) * mm, "end": v(81.66, 199.47) * mm});
            skLineSegment(sketch, "E737", {"start": v(51.31, 183.2) * mm, "end": v(39.54, 167.48) * mm});
            skLineSegment(sketch, "E738", {"start": v(18.02, 218.67) * mm, "end": v(21.2, 218.67) * mm});
            skLineSegment(sketch, "E739", {"start": v(21.2, 212) * mm, "end": v(21.2, 210.8) * mm});
            skLineSegment(sketch, "E740", {"start": v(21.2, 204.13) * mm, "end": v(18.02, 204.13) * mm});
            skLineSegment(sketch, "E741", {"start": v(-15.44, 213.56) * mm, "end": v(-15.44, 162.7) * mm});
            skLineSegment(sketch, "E742", {"start": v(-13.85, 190.06) * mm, "end": v(-13.85, 208.48) * mm});
            skLineSegment(sketch, "E743", {"start": v(-8.77, 184.98) * mm, "end": v(-7.56, 184.98) * mm});
            skLineSegment(sketch, "E744", {"start": v(-2.48, 208.48) * mm, "end": v(-2.48, 190.06) * mm});
            skLineSegment(sketch, "E745", {"start": v(-0.9, 194.1) * mm, "end": v(-0.9, 213.56) * mm});
            skLineSegment(sketch, "E746", {"start": v(11.45, 185.37) * mm, "end": v(2.15, 189.44) * mm});
            skLineSegment(sketch, "E747", {"start": v(31.24, 199.48) * mm, "end": v(16.94, 186.29) * mm});
            skLineSegment(sketch, "E748", {"start": v(15.05, 182.38) * mm, "end": v(28.58, 194.87) * mm});
            skLineSegment(sketch, "E749", {"start": v(14.76, 175.2) * mm, "end": v(15.58, 174.32) * mm});
            skLineSegment(sketch, "E750", {"start": v(36.29, 186.52) * mm, "end": v(22.75, 174.03) * mm});
            skLineSegment(sketch, "E751", {"start": v(3.72, 154.3) * mm, "end": v(41.1, 188.8) * mm});
            skLineSegment(sketch, "E752", {"start": v(-15.44, 213.56) * mm, "end": v(-15.44, 216.73) * mm});
            skLineSegment(sketch, "E753", {"start": v(-0.9, 216.73) * mm, "end": v(-0.9, 213.56) * mm});
            skLineSegment(sketch, "E754", {"start": v(-7.56, 213.56) * mm, "end": v(-8.77, 213.56) * mm});
            skLineSegment(sketch, "E755", {"start": v(36.58, 193.7) * mm, "end": v(35.76, 194.58) * mm});
            skLineSegment(sketch, "E756", {"start": v(31.24, 199.48) * mm, "end": v(32.04, 200.22) * mm});
            skLineSegment(sketch, "E757", {"start": v(32.04, 200.22) * mm, "end": v(32.74, 200.87) * mm});
            skLineSegment(sketch, "E758", {"start": v(32.74, 200.87) * mm, "end": v(33.26, 201.35) * mm});
            skLineSegment(sketch, "E759", {"start": v(33.26, 201.35) * mm, "end": v(33.54, 201.6) * mm});
            skLineSegment(sketch, "E760", {"start": v(33.54, 201.6) * mm, "end": v(33.57, 201.64) * mm});
            skLineSegment(sketch, "E761", {"start": v(43.43, 190.95) * mm, "end": v(43.4, 190.92) * mm});
            skLineSegment(sketch, "E762", {"start": v(43.4, 190.92) * mm, "end": v(43.12, 190.66) * mm});
            skLineSegment(sketch, "E763", {"start": v(43.12, 190.66) * mm, "end": v(42.6, 190.18) * mm});
            skLineSegment(sketch, "E764", {"start": v(42.6, 190.18) * mm, "end": v(41.9, 189.53) * mm});
            skLineSegment(sketch, "E765", {"start": v(41.9, 189.53) * mm, "end": v(41.1, 188.8) * mm});
            skLineSegment(sketch, "E766", {"start": v(-30.94, 137.93) * mm, "end": v(-30.94, 87.07) * mm});
            skLineSegment(sketch, "E767", {"start": v(-29.35, 114.43) * mm, "end": v(-29.35, 132.85) * mm});
            skLineSegment(sketch, "E768", {"start": v(-24.27, 109.35) * mm, "end": v(-23.07, 109.35) * mm});
            skLineSegment(sketch, "E769", {"start": v(-17.99, 132.85) * mm, "end": v(-17.99, 114.43) * mm});
            skLineSegment(sketch, "E770", {"start": v(-16.4, 118.47) * mm, "end": v(-16.4, 137.93) * mm});
            skLineSegment(sketch, "E771", {"start": v(-4.05, 109.74) * mm, "end": v(-13.36, 113.82) * mm});
            skLineSegment(sketch, "E772", {"start": v(15.73, 123.86) * mm, "end": v(1.43, 110.66) * mm});
            skLineSegment(sketch, "E773", {"start": v(-0.46, 106.76) * mm, "end": v(13.08, 119.25) * mm});
            skLineSegment(sketch, "E774", {"start": v(-0.75, 99.58) * mm, "end": v(0.07, 98.7) * mm});
            skLineSegment(sketch, "E775", {"start": v(20.78, 110.9) * mm, "end": v(7.25, 98.4) * mm});
            skLineSegment(sketch, "E776", {"start": v(-11.79, 78.68) * mm, "end": v(25.6, 113.17) * mm});
            skLineSegment(sketch, "E777", {"start": v(-23.07, 137.93) * mm, "end": v(-24.27, 137.93) * mm});
            skLineSegment(sketch, "E778", {"start": v(-30.94, 137.93) * mm, "end": v(-30.94, 141.1) * mm});
            skLineSegment(sketch, "E779", {"start": v(-16.4, 141.1) * mm, "end": v(-16.4, 137.93) * mm});
            skLineSegment(sketch, "E780", {"start": v(21.07, 118.07) * mm, "end": v(20.25, 118.96) * mm});
            skLineSegment(sketch, "E781", {"start": v(15.73, 123.86) * mm, "end": v(16.53, 124.6) * mm});
            skLineSegment(sketch, "E782", {"start": v(16.53, 124.6) * mm, "end": v(17.23, 125.24) * mm});
            skLineSegment(sketch, "E783", {"start": v(17.23, 125.24) * mm, "end": v(17.75, 125.72) * mm});
            skLineSegment(sketch, "E784", {"start": v(17.75, 125.72) * mm, "end": v(18.03, 125.98) * mm});
            skLineSegment(sketch, "E785", {"start": v(18.03, 125.98) * mm, "end": v(18.07, 126.01) * mm});
            skLineSegment(sketch, "E786", {"start": v(27.93, 115.33) * mm, "end": v(27.9, 115.3) * mm});
            skLineSegment(sketch, "E787", {"start": v(27.9, 115.3) * mm, "end": v(27.61, 115.04) * mm});
            skLineSegment(sketch, "E788", {"start": v(27.61, 115.04) * mm, "end": v(27.1, 114.56) * mm});
            skLineSegment(sketch, "E789", {"start": v(27.1, 114.56) * mm, "end": v(26.4, 113.9) * mm});
            skLineSegment(sketch, "E790", {"start": v(26.4, 113.9) * mm, "end": v(25.6, 113.17) * mm});
            skArc(sketch, "E791", {"start": v(148.34, 59.28) * mm, "mid": v(150.44, 62.26) * mm, "end": v(149.8, 65.85) * mm});
            skArc(sketch, "E792", {"start": v(147.93, 57.13) * mm, "mid": v(145.9, 51.78) * mm, "end": v(150.48, 48.35) * mm});
            skArc(sketch, "E793", {"start": v(156.74, 42) * mm, "mid": v(155.35, 45.37) * mm, "end": v(151.98, 46.76) * mm});
            skArc(sketch, "E794", {"start": v(139.28, 46.76) * mm, "mid": v(135.91, 45.37) * mm, "end": v(134.52, 42) * mm});
            skArc(sketch, "E795", {"start": v(134.52, 40.16) * mm, "mid": v(135.91, 36.8) * mm, "end": v(139.28, 35.4) * mm});
            skArc(sketch, "E796", {"start": v(151.98, 35.4) * mm, "mid": v(155.35, 36.8) * mm, "end": v(156.74, 40.16) * mm});
            skArc(sketch, "E797", {"start": v(119, 33.8) * mm, "mid": v(117.04, 33.5) * mm, "end": v(115.27, 32.6) * mm});
            skArc(sketch, "E798", {"start": v(109.76, 51.54) * mm, "mid": v(99.06, 38.15) * mm, "end": v(115.27, 32.6) * mm});
            skArc(sketch, "E799", {"start": v(109.76, 51.54) * mm, "mid": v(111.74, 51.72) * mm, "end": v(113.56, 52.51) * mm});
            skArc(sketch, "E800", {"start": v(148.82, 67.4) * mm, "mid": v(145.84, 69.5) * mm, "end": v(142.25, 68.87) * mm});
            skArc(sketch, "E801", {"start": v(131.53, 62.05) * mm, "mid": v(129.43, 59.07) * mm, "end": v(130.06, 55.48) * mm});
            skArc(sketch, "E802", {"start": v(131.05, 53.93) * mm, "mid": v(134.03, 51.83) * mm, "end": v(137.62, 52.46) * mm});
            skCircle(sketch, "E803", {"center": v(-25.46, 1.07) * mm, "radius": 8.16 * mm});
            skArc(sketch, "E804", {"start": v(165.64, 211.44) * mm, "mid": v(167.73, 214.42) * mm, "end": v(167.1, 218.01) * mm});
            skArc(sketch, "E805", {"start": v(249.94, 59.28) * mm, "mid": v(252.04, 62.26) * mm, "end": v(251.4, 65.85) * mm});
            skArc(sketch, "E806", {"start": v(249.53, 57.13) * mm, "mid": v(247.5, 51.78) * mm, "end": v(252.08, 48.35) * mm});
            skArc(sketch, "E807", {"start": v(258.34, 42) * mm, "mid": v(256.95, 45.37) * mm, "end": v(253.58, 46.76) * mm});
            skArc(sketch, "E808", {"start": v(240.88, 46.76) * mm, "mid": v(237.51, 45.37) * mm, "end": v(236.12, 42) * mm});
            skArc(sketch, "E809", {"start": v(236.12, 40.16) * mm, "mid": v(237.51, 36.8) * mm, "end": v(240.88, 35.4) * mm});
            skArc(sketch, "E810", {"start": v(253.58, 35.4) * mm, "mid": v(256.95, 36.8) * mm, "end": v(258.34, 40.16) * mm});
            skArc(sketch, "E811", {"start": v(220.6, 33.8) * mm, "mid": v(218.64, 33.5) * mm, "end": v(216.87, 32.6) * mm});
            skArc(sketch, "E812", {"start": v(211.36, 51.54) * mm, "mid": v(200.66, 38.15) * mm, "end": v(216.87, 32.6) * mm});
            skArc(sketch, "E813", {"start": v(211.36, 51.54) * mm, "mid": v(213.34, 51.72) * mm, "end": v(215.16, 52.51) * mm});
            skArc(sketch, "E814", {"start": v(250.42, 67.4) * mm, "mid": v(247.44, 69.5) * mm, "end": v(243.85, 68.87) * mm});
            skArc(sketch, "E815", {"start": v(233.13, 62.05) * mm, "mid": v(231.03, 59.07) * mm, "end": v(231.66, 55.48) * mm});
            skArc(sketch, "E816", {"start": v(232.65, 53.93) * mm, "mid": v(235.63, 51.83) * mm, "end": v(239.22, 52.46) * mm});
            skCircle(sketch, "E817", {"center": v(64.22, 59.24) * mm, "radius": 8.16 * mm});
            skArc(sketch, "E818", {"start": v(165.22, 209.3) * mm, "mid": v(163.2, 203.94) * mm, "end": v(167.78, 200.51) * mm});
            skArc(sketch, "E819", {"start": v(181.8, -63.27) * mm, "mid": v(182.42, -61.74) * mm, "end": v(182.51, -60.1) * mm});
            skArc(sketch, "E820", {"start": v(183.83, -8.8) * mm, "mid": v(180.4, -10.66) * mm, "end": v(179.3, -14.4) * mm});
            skArc(sketch, "E821", {"start": v(181.9, -39.02) * mm, "mid": v(183.75, -42.44) * mm, "end": v(187.48, -43.54) * mm});
            skArc(sketch, "E822", {"start": v(188.67, -43.42) * mm, "mid": v(192.1, -41.56) * mm, "end": v(193.2, -37.83) * mm});
            skArc(sketch, "E823", {"start": v(190.6, -13.2) * mm, "mid": v(188.75, -9.79) * mm, "end": v(185.02, -8.68) * mm});
            skArc(sketch, "E824", {"start": v(193.77, -28.08) * mm, "mid": v(194.55, -30.3) * mm, "end": v(196.26, -31.94) * mm});
            skArc(sketch, "E825", {"start": v(220, -45.75) * mm, "mid": v(222.26, -46.43) * mm, "end": v(224.59, -46.02) * mm});
            skArc(sketch, "E826", {"start": v(216.39, -51.33) * mm, "mid": v(213.7, -54.13) * mm, "end": v(213.77, -58.02) * mm});
            skArc(sketch, "E827", {"start": v(214.25, -59.12) * mm, "mid": v(217.05, -61.82) * mm, "end": v(220.94, -61.74) * mm});
            skArc(sketch, "E828", {"start": v(243.63, -51.83) * mm, "mid": v(246.33, -49.03) * mm, "end": v(246.25, -45.14) * mm});
            skArc(sketch, "E829", {"start": v(202.31, -71.61) * mm, "mid": v(200.92, -72.51) * mm, "end": v(199.9, -73.81) * mm});
            skArc(sketch, "E830", {"start": v(181.8, -63.27) * mm, "mid": v(185.46, -77.8) * mm, "end": v(199.9, -73.81) * mm});
            skArc(sketch, "E831", {"start": v(212.99, -49.35) * mm, "mid": v(214.89, -46.62) * mm, "end": v(213.31, -43.7) * mm});
            skArc(sketch, "E832", {"start": v(201.35, -36.73) * mm, "mid": v(198.03, -36.81) * mm, "end": v(196.6, -39.81) * mm});
            skArc(sketch, "E833", {"start": v(197.82, -51.46) * mm, "mid": v(199.38, -53.88) * mm, "end": v(202.25, -54.04) * mm});
            skCircle(sketch, "E834", {"center": v(59.78, 10.52) * mm, "radius": 8.16 * mm});
            skArc(sketch, "E835", {"start": v(245.77, -44.04) * mm, "mid": v(242.97, -41.34) * mm, "end": v(239.08, -41.42) * mm});
            skArc(sketch, "E836", {"start": v(174.04, 194.16) * mm, "mid": v(172.65, 197.53) * mm, "end": v(169.28, 198.92) * mm});
            skArc(sketch, "E837", {"start": v(102.65, -61.42) * mm, "mid": v(103.28, -59.89) * mm, "end": v(103.37, -58.24) * mm});
            skArc(sketch, "E838", {"start": v(104.69, -6.95) * mm, "mid": v(101.27, -8.8) * mm, "end": v(100.17, -12.54) * mm});
            skArc(sketch, "E839", {"start": v(102.75, -37.17) * mm, "mid": v(104.6, -40.58) * mm, "end": v(108.34, -41.69) * mm});
            skArc(sketch, "E840", {"start": v(109.54, -41.56) * mm, "mid": v(112.95, -39.7) * mm, "end": v(114.06, -35.98) * mm});
            skArc(sketch, "E841", {"start": v(111.47, -11.35) * mm, "mid": v(109.61, -7.93) * mm, "end": v(105.88, -6.83) * mm});
            skArc(sketch, "E842", {"start": v(114.63, -26.22) * mm, "mid": v(115.41, -28.45) * mm, "end": v(117.12, -30.08) * mm});
            skArc(sketch, "E843", {"start": v(140.86, -43.9) * mm, "mid": v(143.12, -44.58) * mm, "end": v(145.45, -44.16) * mm});
            skArc(sketch, "E844", {"start": v(137.25, -49.48) * mm, "mid": v(134.55, -52.28) * mm, "end": v(134.63, -56.17) * mm});
            skArc(sketch, "E845", {"start": v(135.1, -57.27) * mm, "mid": v(137.9, -59.96) * mm, "end": v(141.8, -59.9) * mm});
            skArc(sketch, "E846", {"start": v(164.5, -49.98) * mm, "mid": v(167.19, -47.17) * mm, "end": v(167.11, -43.29) * mm});
            skArc(sketch, "E847", {"start": v(123.17, -69.76) * mm, "mid": v(121.79, -70.66) * mm, "end": v(120.76, -71.96) * mm});
            skArc(sketch, "E848", {"start": v(102.65, -61.42) * mm, "mid": v(106.32, -75.94) * mm, "end": v(120.76, -71.96) * mm});
            skArc(sketch, "E849", {"start": v(133.85, -47.5) * mm, "mid": v(135.75, -44.77) * mm, "end": v(134.17, -41.84) * mm});
            skArc(sketch, "E850", {"start": v(122.21, -34.88) * mm, "mid": v(118.9, -34.96) * mm, "end": v(117.46, -37.96) * mm});
            skArc(sketch, "E851", {"start": v(118.68, -49.6) * mm, "mid": v(120.24, -52.02) * mm, "end": v(123.11, -52.19) * mm});
            skCircle(sketch, "E852", {"center": v(109.12, 41.08) * mm, "radius": 8.16 * mm});
            skArc(sketch, "E853", {"start": v(166.63, -42.18) * mm, "mid": v(163.83, -39.49) * mm, "end": v(159.94, -39.56) * mm});
            skArc(sketch, "E854", {"start": v(156.58, 198.92) * mm, "mid": v(153.21, 197.53) * mm, "end": v(151.82, 194.16) * mm});
            skArc(sketch, "E855", {"start": v(55.77, 20.2) * mm, "mid": v(57.17, 21.07) * mm, "end": v(58.22, 22.34) * mm});
            skArc(sketch, "E856", {"start": v(89.42, 63.06) * mm, "mid": v(85.57, 63.57) * mm, "end": v(82.48, 61.2) * mm});
            skArc(sketch, "E857", {"start": v(70.1, 39.75) * mm, "mid": v(69.6, 35.9) * mm, "end": v(71.96, 32.81) * mm});
            skArc(sketch, "E858", {"start": v(73, 32.21) * mm, "mid": v(76.86, 31.7) * mm, "end": v(79.94, 34.07) * mm});
            skArc(sketch, "E859", {"start": v(92.33, 55.52) * mm, "mid": v(92.83, 59.37) * mm, "end": v(90.47, 62.46) * mm});
            skArc(sketch, "E860", {"start": v(86.32, 41.94) * mm, "mid": v(85.64, 39.4) * mm, "end": v(86.32, 36.86) * mm});
            skArc(sketch, "E861", {"start": v(95.86, 20.32) * mm, "mid": v(97.72, 18.47) * mm, "end": v(100.26, 17.78) * mm});
            skArc(sketch, "E862", {"start": v(120.1, 11.12) * mm, "mid": v(118.62, 14.7) * mm, "end": v(115.03, 16.2) * mm});
            skArc(sketch, "E863", {"start": v(90.26, 16.2) * mm, "mid": v(86.67, 14.7) * mm, "end": v(85.18, 11.12) * mm});
            skArc(sketch, "E864", {"start": v(85.18, 9.91) * mm, "mid": v(86.67, 6.32) * mm, "end": v(90.26, 4.83) * mm});
            skArc(sketch, "E865", {"start": v(115.03, 4.83) * mm, "mid": v(118.62, 6.32) * mm, "end": v(120.1, 9.91) * mm});
            skArc(sketch, "E866", {"start": v(69.24, 3.25) * mm, "mid": v(67.61, 2.98) * mm, "end": v(66.15, 2.2) * mm});
            skArc(sketch, "E867", {"start": v(55.77, 20.2) * mm, "mid": v(50.7, 5.28) * mm, "end": v(66.15, 2.2) * mm});
            skArc(sketch, "E868", {"start": v(89.08, 19.37) * mm, "mid": v(91.83, 20.96) * mm, "end": v(91.83, 24.14) * mm});
            skArc(sketch, "E869", {"start": v(87.6, 31.46) * mm, "mid": v(84.85, 33.04) * mm, "end": v(82.1, 31.46) * mm});
            skArc(sketch, "E870", {"start": v(77.87, 24.14) * mm, "mid": v(77.87, 20.96) * mm, "end": v(80.62, 19.37) * mm});
            skCircle(sketch, "E871", {"center": v(161.38, 10.52) * mm, "radius": 8.16 * mm});
            skCircle(sketch, "E872", {"center": v(210.72, 41.08) * mm, "radius": 8.16 * mm});
            skArc(sketch, "E873", {"start": v(157.37, 20.2) * mm, "mid": v(158.77, 21.07) * mm, "end": v(159.82, 22.34) * mm});
            skArc(sketch, "E874", {"start": v(191.02, 63.06) * mm, "mid": v(187.17, 63.57) * mm, "end": v(184.08, 61.2) * mm});
            skArc(sketch, "E875", {"start": v(171.7, 39.75) * mm, "mid": v(171.2, 35.9) * mm, "end": v(173.56, 32.81) * mm});
            skArc(sketch, "E876", {"start": v(174.6, 32.21) * mm, "mid": v(178.46, 31.7) * mm, "end": v(181.54, 34.07) * mm});
            skArc(sketch, "E877", {"start": v(193.93, 55.52) * mm, "mid": v(194.43, 59.37) * mm, "end": v(192.07, 62.46) * mm});
            skArc(sketch, "E878", {"start": v(187.92, 41.94) * mm, "mid": v(187.24, 39.4) * mm, "end": v(187.92, 36.86) * mm});
            skArc(sketch, "E879", {"start": v(197.46, 20.32) * mm, "mid": v(199.32, 18.47) * mm, "end": v(201.86, 17.78) * mm});
            skArc(sketch, "E880", {"start": v(221.7, 11.12) * mm, "mid": v(220.22, 14.7) * mm, "end": v(216.63, 16.2) * mm});
            skArc(sketch, "E881", {"start": v(191.86, 16.2) * mm, "mid": v(188.27, 14.7) * mm, "end": v(186.78, 11.12) * mm});
            skArc(sketch, "E882", {"start": v(186.78, 9.91) * mm, "mid": v(188.27, 6.32) * mm, "end": v(191.86, 4.83) * mm});
            skArc(sketch, "E883", {"start": v(216.63, 4.83) * mm, "mid": v(220.22, 6.32) * mm, "end": v(221.7, 9.91) * mm});
            skArc(sketch, "E884", {"start": v(170.84, 3.25) * mm, "mid": v(169.21, 2.98) * mm, "end": v(167.75, 2.2) * mm});
            skArc(sketch, "E885", {"start": v(157.37, 20.2) * mm, "mid": v(152.3, 5.28) * mm, "end": v(167.75, 2.2) * mm});
            skArc(sketch, "E886", {"start": v(190.68, 19.37) * mm, "mid": v(193.43, 20.96) * mm, "end": v(193.43, 24.14) * mm});
            skArc(sketch, "E887", {"start": v(189.2, 31.46) * mm, "mid": v(186.45, 33.04) * mm, "end": v(183.7, 31.46) * mm});
            skArc(sketch, "E888", {"start": v(179.47, 24.14) * mm, "mid": v(179.47, 20.96) * mm, "end": v(182.22, 19.37) * mm});
            skCircle(sketch, "E889", {"center": v(190.73, -68.74) * mm, "radius": 8.16 * mm});
            skArc(sketch, "E890", {"start": v(151.82, 192.32) * mm, "mid": v(153.21, 188.96) * mm, "end": v(156.58, 187.56) * mm});
            skArc(sketch, "E891", {"start": v(84.48, -22.62) * mm, "mid": v(82.99, -23.32) * mm, "end": v(81.8, -24.47) * mm});
            skArc(sketch, "E892", {"start": v(45.97, -61.18) * mm, "mid": v(49.73, -62.15) * mm, "end": v(53.08, -60.16) * mm});
            skArc(sketch, "E893", {"start": v(67.92, -40.34) * mm, "mid": v(68.89, -36.57) * mm, "end": v(66.9, -33.23) * mm});
            skArc(sketch, "E894", {"start": v(65.94, -32.5) * mm, "mid": v(62.17, -31.54) * mm, "end": v(58.83, -33.53) * mm});
            skArc(sketch, "E895", {"start": v(43.98, -53.35) * mm, "mid": v(43.02, -57.12) * mm, "end": v(45, -60.46) * mm});
            skArc(sketch, "E896", {"start": v(51.44, -40.74) * mm, "mid": v(52.43, -38.15) * mm, "end": v(51.92, -35.43) * mm});
            skArc(sketch, "E897", {"start": v(45.5, -22.61) * mm, "mid": v(43.63, -20.56) * mm, "end": v(40.96, -19.8) * mm});
            skArc(sketch, "E898", {"start": v(21.32, -13.14) * mm, "mid": v(22.8, -16.73) * mm, "end": v(26.4, -18.22) * mm});
            skArc(sketch, "E899", {"start": v(51.17, -18.22) * mm, "mid": v(54.76, -16.73) * mm, "end": v(56.25, -13.14) * mm});
            skArc(sketch, "E900", {"start": v(56.25, -11.94) * mm, "mid": v(54.76, -8.34) * mm, "end": v(51.17, -6.86) * mm});
            skArc(sketch, "E901", {"start": v(26.4, -6.86) * mm, "mid": v(22.8, -8.34) * mm, "end": v(21.32, -11.94) * mm});
            skArc(sketch, "E902", {"start": v(72.18, -5.27) * mm, "mid": v(73.82, -5) * mm, "end": v(75.27, -4.22) * mm});
            skArc(sketch, "E903", {"start": v(84.48, -22.62) * mm, "mid": v(91.02, -7.85) * mm, "end": v(75.27, -4.22) * mm});
            skArc(sketch, "E904", {"start": v(51.81, -21.4) * mm, "mid": v(49.1, -22.9) * mm, "end": v(48.97, -26) * mm});
            skArc(sketch, "E905", {"start": v(51.3, -30.63) * mm, "mid": v(53.85, -32.37) * mm, "end": v(56.67, -31.1) * mm});
            skArc(sketch, "E906", {"start": v(60.14, -26.47) * mm, "mid": v(60.44, -23.15) * mm, "end": v(57.6, -21.4) * mm});
            skCircle(sketch, "E907", {"center": v(111.6, -66.89) * mm, "radius": 8.16 * mm});
            skArc(sketch, "E908", {"start": v(169.28, 187.56) * mm, "mid": v(172.65, 188.96) * mm, "end": v(174.04, 192.32) * mm});
            skArc(sketch, "E909", {"start": v(67.06, 49.15) * mm, "mid": v(65.56, 48.45) * mm, "end": v(64.37, 47.3) * mm});
            skArc(sketch, "E910", {"start": v(28.54, 10.6) * mm, "mid": v(32.3, 9.63) * mm, "end": v(35.65, 11.62) * mm});
            skArc(sketch, "E911", {"start": v(50.5, 31.44) * mm, "mid": v(51.46, 35.2) * mm, "end": v(49.48, 38.55) * mm});
            skArc(sketch, "E912", {"start": v(48.51, 39.27) * mm, "mid": v(44.74, 40.23) * mm, "end": v(41.4, 38.25) * mm});
            skArc(sketch, "E913", {"start": v(26.56, 18.43) * mm, "mid": v(25.6, 14.66) * mm, "end": v(27.58, 11.32) * mm});
            skArc(sketch, "E914", {"start": v(34.01, 31.03) * mm, "mid": v(35, 33.63) * mm, "end": v(34.49, 36.35) * mm});
            skArc(sketch, "E915", {"start": v(28.08, 49.16) * mm, "mid": v(26.2, 51.21) * mm, "end": v(23.54, 51.97) * mm});
            skArc(sketch, "E916", {"start": v(3.9, 58.64) * mm, "mid": v(5.38, 55.05) * mm, "end": v(8.97, 53.56) * mm});
            skArc(sketch, "E917", {"start": v(33.74, 53.56) * mm, "mid": v(37.33, 55.05) * mm, "end": v(38.82, 58.64) * mm});
            skArc(sketch, "E918", {"start": v(38.82, 59.84) * mm, "mid": v(37.33, 63.43) * mm, "end": v(33.74, 64.92) * mm});
            skArc(sketch, "E919", {"start": v(8.97, 64.92) * mm, "mid": v(5.38, 63.43) * mm, "end": v(3.9, 59.84) * mm});
            skArc(sketch, "E920", {"start": v(54.76, 66.5) * mm, "mid": v(56.39, 66.78) * mm, "end": v(57.85, 67.56) * mm});
            skArc(sketch, "E921", {"start": v(67.06, 49.15) * mm, "mid": v(73.59, 63.93) * mm, "end": v(57.85, 67.56) * mm});
            skArc(sketch, "E922", {"start": v(34.38, 50.38) * mm, "mid": v(31.68, 48.88) * mm, "end": v(31.54, 45.79) * mm});
            skArc(sketch, "E923", {"start": v(33.86, 41.15) * mm, "mid": v(36.42, 39.4) * mm, "end": v(39.24, 40.67) * mm});
            skArc(sketch, "E924", {"start": v(42.72, 45.3) * mm, "mid": v(43.01, 48.63) * mm, "end": v(40.17, 50.38) * mm});
            skCircle(sketch, "E925", {"center": v(-8.04, -70.71) * mm, "radius": 8.16 * mm});
            skCircle(sketch, "E926", {"center": v(81.65, -12.54) * mm, "radius": 8.16 * mm});
            skArc(sketch, "E927", {"start": v(-33.78, 7.44) * mm, "mid": v(-33, 8.9) * mm, "end": v(-32.73, 10.53) * mm});
            skArc(sketch, "E928", {"start": v(-26.07, 61.4) * mm, "mid": v(-29.66, 59.9) * mm, "end": v(-31.15, 56.31) * mm});
            skArc(sketch, "E929", {"start": v(-31.15, 37.9) * mm, "mid": v(-29.66, 34.3) * mm, "end": v(-26.07, 32.82) * mm});
            skArc(sketch, "E930", {"start": v(-24.86, 32.82) * mm, "mid": v(-21.27, 34.3) * mm, "end": v(-19.78, 37.9) * mm});
            skArc(sketch, "E931", {"start": v(-19.78, 56.31) * mm, "mid": v(-21.27, 59.9) * mm, "end": v(-24.86, 61.4) * mm});
            skArc(sketch, "E932", {"start": v(-18.2, 41.93) * mm, "mid": v(-17.37, 39.15) * mm, "end": v(-15.15, 37.28) * mm});
            skArc(sketch, "E933", {"start": v(-5.84, 33.2) * mm, "mid": v(-2.97, 32.85) * mm, "end": v(-0.36, 34.12) * mm});
            skArc(sketch, "E934", {"start": v(18.46, 42.42) * mm, "mid": v(14.93, 44.05) * mm, "end": v(11.28, 42.7) * mm});
            skArc(sketch, "E935", {"start": v(-2.25, 30.22) * mm, "mid": v(-3.88, 26.69) * mm, "end": v(-2.54, 23.04) * mm});
            skArc(sketch, "E936", {"start": v(-1.72, 22.16) * mm, "mid": v(1.8, 20.52) * mm, "end": v(5.46, 21.87) * mm});
            skArc(sketch, "E937", {"start": v(18.99, 34.36) * mm, "mid": v(20.62, 37.88) * mm, "end": v(19.28, 41.53) * mm});
            skArc(sketch, "E938", {"start": v(-13.58, 2.14) * mm, "mid": v(-14.6, 0.84) * mm, "end": v(-15.14, -0.72) * mm});
            skArc(sketch, "E939", {"start": v(-33.78, 7.44) * mm, "mid": v(-29.67, -8.53) * mm, "end": v(-15.14, -0.72) * mm});
            skArc(sketch, "E940", {"start": v(136.3, 185.97) * mm, "mid": v(134.34, 185.66) * mm, "end": v(132.57, 184.76) * mm});
            skArc(sketch, "E941", {"start": v(127.06, 203.7) * mm, "mid": v(116.36, 190.32) * mm, "end": v(132.57, 184.76) * mm});
            skArc(sketch, "E942", {"start": v(-16.35, -64.34) * mm, "mid": v(-15.58, -62.88) * mm, "end": v(-15.3, -61.25) * mm});
            skArc(sketch, "E943", {"start": v(-8.64, -10.39) * mm, "mid": v(-12.23, -11.87) * mm, "end": v(-13.72, -15.47) * mm});
            skArc(sketch, "E944", {"start": v(-13.72, -33.88) * mm, "mid": v(-12.23, -37.47) * mm, "end": v(-8.64, -38.96) * mm});
            skArc(sketch, "E945", {"start": v(-7.44, -38.96) * mm, "mid": v(-3.84, -37.47) * mm, "end": v(-2.36, -33.88) * mm});
            skArc(sketch, "E946", {"start": v(-2.36, -15.47) * mm, "mid": v(-3.84, -11.87) * mm, "end": v(-7.44, -10.39) * mm});
            skArc(sketch, "E947", {"start": v(-0.77, -29.84) * mm, "mid": v(0.06, -32.62) * mm, "end": v(2.27, -34.5) * mm});
            skArc(sketch, "E948", {"start": v(11.58, -38.57) * mm, "mid": v(14.46, -38.93) * mm, "end": v(17.07, -37.65) * mm});
            skArc(sketch, "E949", {"start": v(35.89, -29.36) * mm, "mid": v(32.36, -27.73) * mm, "end": v(28.7, -29.07) * mm});
            skArc(sketch, "E950", {"start": v(15.18, -41.56) * mm, "mid": v(13.55, -45.09) * mm, "end": v(14.89, -48.74) * mm});
            skArc(sketch, "E951", {"start": v(15.7, -49.62) * mm, "mid": v(19.23, -51.25) * mm, "end": v(22.88, -49.91) * mm});
            skArc(sketch, "E952", {"start": v(36.42, -37.42) * mm, "mid": v(38.05, -33.9) * mm, "end": v(36.7, -30.24) * mm});
            skArc(sketch, "E953", {"start": v(3.85, -69.64) * mm, "mid": v(2.83, -70.94) * mm, "end": v(2.29, -72.5) * mm});
            skArc(sketch, "E954", {"start": v(-16.35, -64.34) * mm, "mid": v(-12.24, -80.3) * mm, "end": v(2.29, -72.5) * mm});
            skArc(sketch, "E955", {"start": v(127.06, 203.7) * mm, "mid": v(129.04, 203.89) * mm, "end": v(130.86, 204.68) * mm});
            skArc(sketch, "E956", {"start": v(166.12, 219.56) * mm, "mid": v(163.13, 221.66) * mm, "end": v(159.54, 221.03) * mm});
            skArc(sketch, "E957", {"start": v(148.83, 214.22) * mm, "mid": v(146.73, 211.23) * mm, "end": v(147.36, 207.64) * mm});
            skArc(sketch, "E958", {"start": v(148.35, 206.1) * mm, "mid": v(151.33, 204) * mm, "end": v(154.92, 204.63) * mm});
            skCircle(sketch, "E959", {"center": v(-8.17, 153.23) * mm, "radius": 8.16 * mm});
            skArc(sketch, "E960", {"start": v(254.93, 143.14) * mm, "mid": v(257.02, 146.12) * mm, "end": v(256.4, 149.71) * mm});
            skArc(sketch, "E961", {"start": v(254.51, 141) * mm, "mid": v(252.5, 135.65) * mm, "end": v(257.07, 132.21) * mm});
            skArc(sketch, "E962", {"start": v(263.33, 125.86) * mm, "mid": v(261.94, 129.23) * mm, "end": v(258.57, 130.63) * mm});
            skArc(sketch, "E963", {"start": v(245.87, 130.63) * mm, "mid": v(242.5, 129.23) * mm, "end": v(241.1, 125.86) * mm});
            skArc(sketch, "E964", {"start": v(241.1, 124.02) * mm, "mid": v(242.5, 120.66) * mm, "end": v(245.87, 119.26) * mm});
            skArc(sketch, "E965", {"start": v(258.57, 119.26) * mm, "mid": v(261.94, 120.66) * mm, "end": v(263.33, 124.02) * mm});
            skArc(sketch, "E966", {"start": v(225.59, 117.67) * mm, "mid": v(223.63, 117.36) * mm, "end": v(221.86, 116.46) * mm});
            skArc(sketch, "E967", {"start": v(216.35, 135.4) * mm, "mid": v(205.64, 122.02) * mm, "end": v(221.86, 116.46) * mm});
            skArc(sketch, "E968", {"start": v(216.35, 135.4) * mm, "mid": v(218.33, 135.6) * mm, "end": v(220.15, 136.38) * mm});
            skArc(sketch, "E969", {"start": v(255.4, 151.27) * mm, "mid": v(252.42, 153.36) * mm, "end": v(248.83, 152.73) * mm});
            skArc(sketch, "E970", {"start": v(238.11, 145.92) * mm, "mid": v(236.02, 142.94) * mm, "end": v(236.65, 139.34) * mm});
            skArc(sketch, "E971", {"start": v(237.63, 137.8) * mm, "mid": v(240.62, 135.7) * mm, "end": v(244.2, 136.33) * mm});
            skCircle(sketch, "E972", {"center": v(81.52, 211.4) * mm, "radius": 8.16 * mm});
            skArc(sketch, "E973", {"start": v(166.16, 85.04) * mm, "mid": v(166.78, 86.58) * mm, "end": v(166.88, 88.23) * mm});
            skArc(sketch, "E974", {"start": v(168.2, 139.5) * mm, "mid": v(164.78, 137.65) * mm, "end": v(163.67, 133.92) * mm});
            skArc(sketch, "E975", {"start": v(166.26, 109.3) * mm, "mid": v(168.12, 105.88) * mm, "end": v(171.84, 104.77) * mm});
            skArc(sketch, "E976", {"start": v(173.04, 104.9) * mm, "mid": v(176.46, 106.76) * mm, "end": v(177.56, 110.48) * mm});
            skArc(sketch, "E977", {"start": v(174.97, 135.11) * mm, "mid": v(173.12, 138.53) * mm, "end": v(169.4, 139.63) * mm});
            skArc(sketch, "E978", {"start": v(178.13, 120.24) * mm, "mid": v(178.92, 118.01) * mm, "end": v(180.63, 116.38) * mm});
            skArc(sketch, "E979", {"start": v(204.37, 102.57) * mm, "mid": v(206.63, 101.88) * mm, "end": v(208.95, 102.3) * mm});
            skArc(sketch, "E980", {"start": v(200.75, 96.99) * mm, "mid": v(198.06, 94.18) * mm, "end": v(198.13, 90.3) * mm});
            skArc(sketch, "E981", {"start": v(198.61, 89.2) * mm, "mid": v(201.42, 86.5) * mm, "end": v(205.3, 86.57) * mm});
            skArc(sketch, "E982", {"start": v(228, 96.49) * mm, "mid": v(230.7, 99.29) * mm, "end": v(230.62, 103.18) * mm});
            skArc(sketch, "E983", {"start": v(186.68, 76.7) * mm, "mid": v(185.3, 75.8) * mm, "end": v(184.27, 74.5) * mm});
            skArc(sketch, "E984", {"start": v(166.16, 85.04) * mm, "mid": v(169.83, 70.52) * mm, "end": v(184.27, 74.5) * mm});
            skArc(sketch, "E985", {"start": v(197.35, 98.97) * mm, "mid": v(199.25, 101.7) * mm, "end": v(197.68, 104.62) * mm});
            skArc(sketch, "E986", {"start": v(185.72, 111.58) * mm, "mid": v(182.4, 111.5) * mm, "end": v(180.96, 108.5) * mm});
            skArc(sketch, "E987", {"start": v(182.19, 96.85) * mm, "mid": v(183.75, 94.44) * mm, "end": v(186.62, 94.28) * mm});
            skCircle(sketch, "E988", {"center": v(77.08, 162.68) * mm, "radius": 8.16 * mm});
            skArc(sketch, "E989", {"start": v(230.14, 104.28) * mm, "mid": v(227.33, 106.97) * mm, "end": v(223.45, 106.9) * mm});
            skArc(sketch, "E990", {"start": v(87.02, 86.9) * mm, "mid": v(87.64, 88.43) * mm, "end": v(87.74, 90.08) * mm});
            skArc(sketch, "E991", {"start": v(89.05, 141.36) * mm, "mid": v(85.64, 139.5) * mm, "end": v(84.53, 135.78) * mm});
            skArc(sketch, "E992", {"start": v(87.12, 111.15) * mm, "mid": v(88.98, 107.73) * mm, "end": v(92.7, 106.63) * mm});
            skArc(sketch, "E993", {"start": v(93.9, 106.75) * mm, "mid": v(97.32, 108.6) * mm, "end": v(98.42, 112.34) * mm});
            skArc(sketch, "E994", {"start": v(95.83, 136.97) * mm, "mid": v(93.98, 140.38) * mm, "end": v(90.25, 141.49) * mm});
            skArc(sketch, "E995", {"start": v(99, 122.1) * mm, "mid": v(99.78, 119.87) * mm, "end": v(101.5, 118.23) * mm});
            skArc(sketch, "E996", {"start": v(125.23, 104.42) * mm, "mid": v(127.49, 103.74) * mm, "end": v(129.82, 104.15) * mm});
            skArc(sketch, "E997", {"start": v(121.61, 98.84) * mm, "mid": v(118.92, 96.04) * mm, "end": v(119, 92.15) * mm});
            skArc(sketch, "E998", {"start": v(119.47, 91.05) * mm, "mid": v(122.28, 88.35) * mm, "end": v(126.16, 88.43) * mm});
            skArc(sketch, "E999", {"start": v(148.86, 98.34) * mm, "mid": v(151.55, 101.14) * mm, "end": v(151.48, 105.03) * mm});
            skArc(sketch, "E1000", {"start": v(107.54, 78.56) * mm, "mid": v(106.15, 77.66) * mm, "end": v(105.13, 76.36) * mm});
            skArc(sketch, "E1001", {"start": v(87.02, 86.9) * mm, "mid": v(90.69, 72.37) * mm, "end": v(105.13, 76.36) * mm});
            skArc(sketch, "E1002", {"start": v(118.21, 100.82) * mm, "mid": v(120.11, 103.55) * mm, "end": v(118.54, 106.47) * mm});
            skArc(sketch, "E1003", {"start": v(106.58, 113.44) * mm, "mid": v(103.26, 113.36) * mm, "end": v(101.82, 110.36) * mm});
            skArc(sketch, "E1004", {"start": v(103.05, 98.7) * mm, "mid": v(104.6, 96.3) * mm, "end": v(107.48, 96.13) * mm});
            skCircle(sketch, "E1005", {"center": v(126.42, 193.24) * mm, "radius": 8.16 * mm});
            skArc(sketch, "E1006", {"start": v(151, 106.13) * mm, "mid": v(148.2, 108.83) * mm, "end": v(144.3, 108.75) * mm});
            skArc(sketch, "E1007", {"start": v(73.06, 172.36) * mm, "mid": v(74.47, 173.23) * mm, "end": v(75.52, 174.5) * mm});
            skArc(sketch, "E1008", {"start": v(106.72, 215.22) * mm, "mid": v(102.87, 215.73) * mm, "end": v(99.78, 213.36) * mm});
            skArc(sketch, "E1009", {"start": v(87.4, 191.92) * mm, "mid": v(86.9, 188.06) * mm, "end": v(89.26, 184.98) * mm});
            skArc(sketch, "E1010", {"start": v(90.3, 184.38) * mm, "mid": v(94.16, 183.87) * mm, "end": v(97.24, 186.23) * mm});
            skArc(sketch, "E1011", {"start": v(109.62, 207.68) * mm, "mid": v(110.13, 211.54) * mm, "end": v(107.76, 214.62) * mm});
            skArc(sketch, "E1012", {"start": v(103.62, 194.1) * mm, "mid": v(102.94, 191.56) * mm, "end": v(103.62, 189.02) * mm});
            skArc(sketch, "E1013", {"start": v(113.16, 172.49) * mm, "mid": v(115.02, 170.63) * mm, "end": v(117.56, 169.95) * mm});
            skArc(sketch, "E1014", {"start": v(137.4, 163.28) * mm, "mid": v(135.92, 166.87) * mm, "end": v(132.33, 168.36) * mm});
            skArc(sketch, "E1015", {"start": v(107.56, 168.36) * mm, "mid": v(103.97, 166.87) * mm, "end": v(102.48, 163.28) * mm});
            skArc(sketch, "E1016", {"start": v(102.48, 162.08) * mm, "mid": v(103.97, 158.49) * mm, "end": v(107.56, 157) * mm});
            skArc(sketch, "E1017", {"start": v(132.33, 157) * mm, "mid": v(135.92, 158.49) * mm, "end": v(137.4, 162.08) * mm});
            skArc(sketch, "E1018", {"start": v(86.54, 155.4) * mm, "mid": v(84.91, 155.14) * mm, "end": v(83.45, 154.36) * mm});
            skArc(sketch, "E1019", {"start": v(73.06, 172.36) * mm, "mid": v(68, 157.44) * mm, "end": v(83.45, 154.36) * mm});
            skArc(sketch, "E1020", {"start": v(106.38, 171.54) * mm, "mid": v(109.13, 173.12) * mm, "end": v(109.13, 176.3) * mm});
            skArc(sketch, "E1021", {"start": v(104.9, 183.62) * mm, "mid": v(102.15, 185.2) * mm, "end": v(99.4, 183.62) * mm});
            skArc(sketch, "E1022", {"start": v(95.17, 176.3) * mm, "mid": v(95.17, 173.12) * mm, "end": v(97.92, 171.54) * mm});
            skCircle(sketch, "E1023", {"center": v(178.68, 162.68) * mm, "radius": 8.16 * mm});
            skCircle(sketch, "E1024", {"center": v(215.7, 124.94) * mm, "radius": 8.16 * mm});
            skArc(sketch, "E1025", {"start": v(174.66, 172.36) * mm, "mid": v(176.07, 173.23) * mm, "end": v(177.12, 174.5) * mm});
            skArc(sketch, "E1026", {"start": v(208.32, 215.22) * mm, "mid": v(204.47, 215.73) * mm, "end": v(201.38, 213.36) * mm});
            skArc(sketch, "E1027", {"start": v(189, 191.92) * mm, "mid": v(188.5, 188.06) * mm, "end": v(190.86, 184.98) * mm});
            skArc(sketch, "E1028", {"start": v(191.9, 184.38) * mm, "mid": v(195.76, 183.87) * mm, "end": v(198.84, 186.23) * mm});
            skArc(sketch, "E1029", {"start": v(211.22, 207.68) * mm, "mid": v(211.73, 211.54) * mm, "end": v(209.36, 214.62) * mm});
            skArc(sketch, "E1030", {"start": v(205.22, 194.1) * mm, "mid": v(204.54, 191.56) * mm, "end": v(205.22, 189.02) * mm});
            skArc(sketch, "E1031", {"start": v(214.76, 172.49) * mm, "mid": v(216.62, 170.63) * mm, "end": v(219.16, 169.95) * mm});
            skArc(sketch, "E1032", {"start": v(239, 163.28) * mm, "mid": v(237.52, 166.87) * mm, "end": v(233.93, 168.36) * mm});
            skArc(sketch, "E1033", {"start": v(209.16, 168.36) * mm, "mid": v(205.57, 166.87) * mm, "end": v(204.08, 163.28) * mm});
            skArc(sketch, "E1034", {"start": v(204.08, 162.08) * mm, "mid": v(205.57, 158.49) * mm, "end": v(209.16, 157) * mm});
            skArc(sketch, "E1035", {"start": v(233.93, 157) * mm, "mid": v(237.52, 158.49) * mm, "end": v(239, 162.08) * mm});
            skArc(sketch, "E1036", {"start": v(188.14, 155.4) * mm, "mid": v(186.51, 155.14) * mm, "end": v(185.05, 154.36) * mm});
            skArc(sketch, "E1037", {"start": v(174.66, 172.36) * mm, "mid": v(169.6, 157.44) * mm, "end": v(185.05, 154.36) * mm});
            skArc(sketch, "E1038", {"start": v(207.98, 171.54) * mm, "mid": v(210.73, 173.12) * mm, "end": v(210.73, 176.3) * mm});
            skArc(sketch, "E1039", {"start": v(206.5, 183.62) * mm, "mid": v(203.75, 185.2) * mm, "end": v(201, 183.62) * mm});
            skArc(sketch, "E1040", {"start": v(196.77, 176.3) * mm, "mid": v(196.77, 173.12) * mm, "end": v(199.52, 171.54) * mm});
            skCircle(sketch, "E1041", {"center": v(175.1, 79.58) * mm, "radius": 8.16 * mm});
            skArc(sketch, "E1042", {"start": v(68.85, 125.7) * mm, "mid": v(67.35, 125) * mm, "end": v(66.16, 123.85) * mm});
            skArc(sketch, "E1043", {"start": v(30.33, 87.13) * mm, "mid": v(34.1, 86.17) * mm, "end": v(37.44, 88.15) * mm});
            skArc(sketch, "E1044", {"start": v(52.3, 107.98) * mm, "mid": v(53.25, 111.74) * mm, "end": v(51.27, 115.09) * mm});
            skArc(sketch, "E1045", {"start": v(50.3, 115.8) * mm, "mid": v(46.54, 116.77) * mm, "end": v(43.2, 114.79) * mm});
            skArc(sketch, "E1046", {"start": v(28.35, 94.97) * mm, "mid": v(27.39, 91.2) * mm, "end": v(29.37, 87.85) * mm});
            skArc(sketch, "E1047", {"start": v(35.8, 107.57) * mm, "mid": v(36.8, 110.16) * mm, "end": v(36.28, 112.9) * mm});
            skArc(sketch, "E1048", {"start": v(29.87, 125.7) * mm, "mid": v(28, 127.75) * mm, "end": v(25.33, 128.5) * mm});
            skArc(sketch, "E1049", {"start": v(5.69, 135.18) * mm, "mid": v(7.18, 131.58) * mm, "end": v(10.77, 130.1) * mm});
            skArc(sketch, "E1050", {"start": v(35.53, 130.1) * mm, "mid": v(39.13, 131.58) * mm, "end": v(40.61, 135.18) * mm});
            skArc(sketch, "E1051", {"start": v(40.61, 136.38) * mm, "mid": v(39.13, 139.97) * mm, "end": v(35.53, 141.46) * mm});
            skArc(sketch, "E1052", {"start": v(10.77, 141.46) * mm, "mid": v(7.18, 139.97) * mm, "end": v(5.69, 136.38) * mm});
            skArc(sketch, "E1053", {"start": v(56.55, 143.05) * mm, "mid": v(58.18, 143.32) * mm, "end": v(59.64, 144.1) * mm});
            skArc(sketch, "E1054", {"start": v(68.85, 125.7) * mm, "mid": v(75.38, 140.47) * mm, "end": v(59.64, 144.1) * mm});
            skArc(sketch, "E1055", {"start": v(36.18, 126.92) * mm, "mid": v(33.48, 125.41) * mm, "end": v(33.34, 122.32) * mm});
            skArc(sketch, "E1056", {"start": v(35.66, 117.69) * mm, "mid": v(38.21, 115.95) * mm, "end": v(41.04, 117.2) * mm});
            skArc(sketch, "E1057", {"start": v(44.5, 121.84) * mm, "mid": v(44.8, 125.17) * mm, "end": v(41.97, 126.92) * mm});
            skCircle(sketch, "E1058", {"center": v(95.96, 81.43) * mm, "radius": 8.16 * mm});
            skArc(sketch, "E1059", {"start": v(84.36, 201.32) * mm, "mid": v(82.86, 200.62) * mm, "end": v(81.66, 199.47) * mm});
            skArc(sketch, "E1060", {"start": v(45.84, 162.76) * mm, "mid": v(49.6, 161.8) * mm, "end": v(52.95, 163.78) * mm});
            skArc(sketch, "E1061", {"start": v(67.8, 183.6) * mm, "mid": v(68.76, 187.37) * mm, "end": v(66.77, 190.71) * mm});
            skArc(sketch, "E1062", {"start": v(65.81, 191.43) * mm, "mid": v(62.04, 192.4) * mm, "end": v(58.7, 190.41) * mm});
            skArc(sketch, "E1063", {"start": v(43.85, 170.6) * mm, "mid": v(42.9, 166.82) * mm, "end": v(44.87, 163.48) * mm});
            skArc(sketch, "E1064", {"start": v(51.31, 183.2) * mm, "mid": v(52.3, 185.79) * mm, "end": v(51.79, 188.52) * mm});
            skArc(sketch, "E1065", {"start": v(45.38, 201.33) * mm, "mid": v(43.5, 203.38) * mm, "end": v(40.83, 204.13) * mm});
            skArc(sketch, "E1066", {"start": v(21.2, 210.8) * mm, "mid": v(22.68, 207.21) * mm, "end": v(26.27, 205.72) * mm});
            skArc(sketch, "E1067", {"start": v(51.04, 205.72) * mm, "mid": v(54.63, 207.21) * mm, "end": v(56.12, 210.8) * mm});
            skArc(sketch, "E1068", {"start": v(56.12, 212) * mm, "mid": v(54.63, 215.6) * mm, "end": v(51.04, 217.09) * mm});
            skArc(sketch, "E1069", {"start": v(26.27, 217.09) * mm, "mid": v(22.68, 215.6) * mm, "end": v(21.2, 212) * mm});
            skArc(sketch, "E1070", {"start": v(72.06, 218.67) * mm, "mid": v(73.69, 218.94) * mm, "end": v(75.15, 219.72) * mm});
            skArc(sketch, "E1071", {"start": v(84.36, 201.32) * mm, "mid": v(90.89, 216.1) * mm, "end": v(75.15, 219.72) * mm});
            skArc(sketch, "E1072", {"start": v(51.68, 202.55) * mm, "mid": v(48.98, 201.04) * mm, "end": v(48.84, 197.95) * mm});
            skArc(sketch, "E1073", {"start": v(51.16, 193.31) * mm, "mid": v(53.72, 191.57) * mm, "end": v(56.54, 192.83) * mm});
            skArc(sketch, "E1074", {"start": v(60.01, 197.47) * mm, "mid": v(60.31, 200.8) * mm, "end": v(57.47, 202.55) * mm});
            skCircle(sketch, "E1075", {"center": v(-23.67, 77.6) * mm, "radius": 8.16 * mm});
            skCircle(sketch, "E1076", {"center": v(66.01, 135.78) * mm, "radius": 8.16 * mm});
            skArc(sketch, "E1077", {"start": v(-16.48, 159.6) * mm, "mid": v(-15.7, 161.06) * mm, "end": v(-15.44, 162.7) * mm});
            skArc(sketch, "E1078", {"start": v(-8.77, 213.56) * mm, "mid": v(-12.36, 212.07) * mm, "end": v(-13.85, 208.48) * mm});
            skArc(sketch, "E1079", {"start": v(-13.85, 190.06) * mm, "mid": v(-12.36, 186.47) * mm, "end": v(-8.77, 184.98) * mm});
            skArc(sketch, "E1080", {"start": v(-7.56, 184.98) * mm, "mid": v(-3.97, 186.47) * mm, "end": v(-2.48, 190.06) * mm});
            skArc(sketch, "E1081", {"start": v(-2.48, 208.48) * mm, "mid": v(-3.97, 212.07) * mm, "end": v(-7.56, 213.56) * mm});
            skArc(sketch, "E1082", {"start": v(-0.9, 194.1) * mm, "mid": v(-0.07, 191.32) * mm, "end": v(2.15, 189.44) * mm});
            skArc(sketch, "E1083", {"start": v(11.45, 185.37) * mm, "mid": v(14.33, 185.01) * mm, "end": v(16.94, 186.29) * mm});
            skArc(sketch, "E1084", {"start": v(35.76, 194.58) * mm, "mid": v(32.23, 196.21) * mm, "end": v(28.58, 194.87) * mm});
            skArc(sketch, "E1085", {"start": v(15.05, 182.38) * mm, "mid": v(13.42, 178.85) * mm, "end": v(14.76, 175.2) * mm});
            skArc(sketch, "E1086", {"start": v(15.58, 174.32) * mm, "mid": v(19.1, 172.69) * mm, "end": v(22.75, 174.03) * mm});
            skArc(sketch, "E1087", {"start": v(36.29, 186.52) * mm, "mid": v(37.92, 190.05) * mm, "end": v(36.58, 193.7) * mm});
            skArc(sketch, "E1088", {"start": v(3.72, 154.3) * mm, "mid": v(2.7, 153) * mm, "end": v(2.16, 151.44) * mm});
            skArc(sketch, "E1089", {"start": v(-16.48, 159.6) * mm, "mid": v(-12.37, 143.63) * mm, "end": v(2.16, 151.44) * mm});
            skArc(sketch, "E1090", {"start": v(-31.99, 83.98) * mm, "mid": v(-31.2, 85.44) * mm, "end": v(-30.94, 87.07) * mm});
            skArc(sketch, "E1091", {"start": v(-24.27, 137.93) * mm, "mid": v(-27.86, 136.44) * mm, "end": v(-29.35, 132.85) * mm});
            skArc(sketch, "E1092", {"start": v(-29.35, 114.43) * mm, "mid": v(-27.86, 110.84) * mm, "end": v(-24.27, 109.35) * mm});
            skArc(sketch, "E1093", {"start": v(-23.07, 109.35) * mm, "mid": v(-19.48, 110.84) * mm, "end": v(-17.99, 114.43) * mm});
            skArc(sketch, "E1094", {"start": v(-17.99, 132.85) * mm, "mid": v(-19.48, 136.44) * mm, "end": v(-23.07, 137.93) * mm});
            skArc(sketch, "E1095", {"start": v(-16.4, 118.47) * mm, "mid": v(-15.57, 115.7) * mm, "end": v(-13.36, 113.82) * mm});
            skArc(sketch, "E1096", {"start": v(-4.05, 109.74) * mm, "mid": v(-1.17, 109.38) * mm, "end": v(1.43, 110.66) * mm});
            skArc(sketch, "E1097", {"start": v(20.25, 118.96) * mm, "mid": v(16.73, 120.59) * mm, "end": v(13.08, 119.25) * mm});
            skArc(sketch, "E1098", {"start": v(-0.46, 106.76) * mm, "mid": v(-2.09, 103.23) * mm, "end": v(-0.75, 99.58) * mm});
            skArc(sketch, "E1099", {"start": v(0.07, 98.7) * mm, "mid": v(3.6, 97.06) * mm, "end": v(7.25, 98.4) * mm});
            skArc(sketch, "E1100", {"start": v(20.78, 110.9) * mm, "mid": v(22.41, 114.42) * mm, "end": v(21.07, 118.07) * mm});
            skArc(sketch, "E1101", {"start": v(-11.79, 78.68) * mm, "mid": v(-12.8, 77.38) * mm, "end": v(-13.35, 75.81) * mm});
            skArc(sketch, "E1102", {"start": v(-31.99, 83.98) * mm, "mid": v(-27.87, 68) * mm, "end": v(-13.35, 75.81) * mm});
            skSolve(sketch);
        }
        {
            var Q0;
            Q0=makeQuery(id+"F2.imprint","IMPRINT",FACE,{"disambiguationData":[TD([[makeQuery(id+"F2.imprint","IMPRINT",EDGE,{"derivedFrom":sQuery(id+"F2.wireOp",EDGE,"E221")}),1.0]])]});
            extrude(context, id + "F3", {"entities" : qUnion([Q0]), "depth" : 6.35 * mm, "offsetDistance" : 25.4 * mm});
        }
    });
